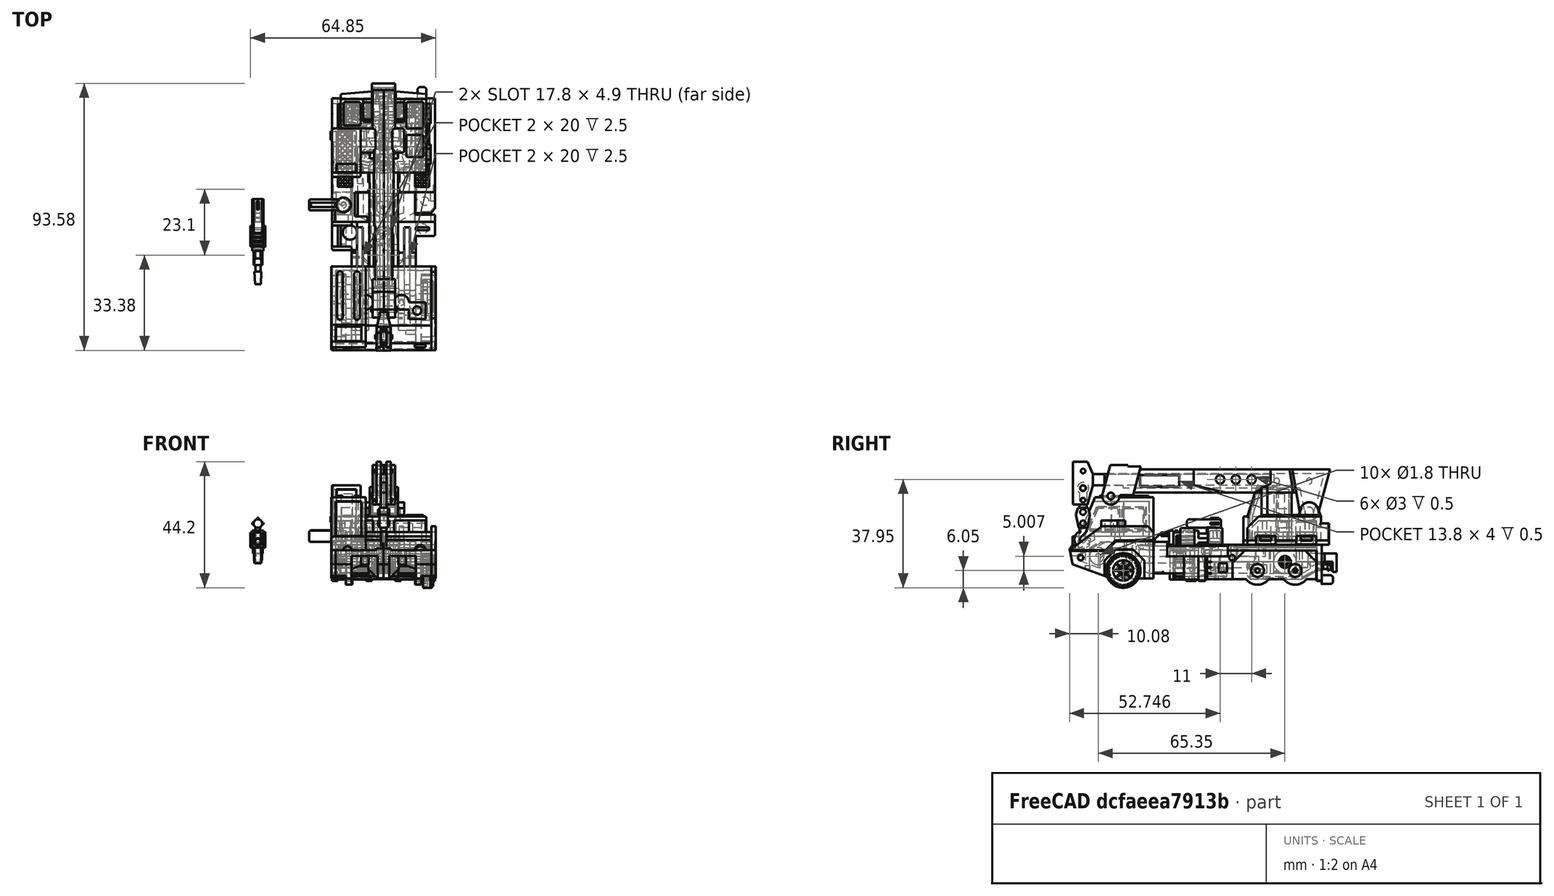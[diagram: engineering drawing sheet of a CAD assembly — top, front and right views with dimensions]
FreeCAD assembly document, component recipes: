
FREECAD ASSEMBLY — COMPONENT RECIPES ("Hook")

This assembly document has 27 components, labeled P0..P26 below (a component is one placed body or linked part). 27 of them carry a construction recipe — the FreeCAD feature program that regenerates the part from scratch, quoted from this document or its linked companion documents; the rest are supplied as boundary geometry only. No exploded tour is included for this assembly.
NOTE — document 3 of 5 of this assembly tour. The two overview renders and the header above are repeated from document 1; the component sections below continue where the previous document stopped.
COMPONENT P13 — recipe-attached ("Legs", modeled in this document).
Construction recipe (the document's own serialized feature program — sketch geometry with constraints, then the solid features built on it; lengths are millimeters unless a unit is written):

FEATURE [PartDesign::SubShapeBinder] Binder009
  BindCopyOnChange = 0
  BindMode = 0
  ClaimChildren = false
  Context = -> Part [Body015.Binder009.]
  Fuse = false
  MakeFace = true
  OffsetFill = false
  OffsetIntersection = false
  OffsetJoinType = 0
  OffsetOpenResult = false
  PartialLoad = false
  Refine = true
  Relative = true
  Support = -> [Body010[Fillet006.Face6]]
  _Version = 2
FEATURE [Sketcher::SketchObject] Sketch213
  ArcFitTolerance = 1e-06
  AttachmentSupport = -> [Binder009]
  ExternalGeometry = -> [Binder009]
  FullyConstrained = true
  MakeInternals = false
  MapMode = 5
  Placement = pos=(0,0,0) rot=(1,0,0;1.5708rad)
  sketch-geometry (4):
    g0: LineSegment StartX=12.75 StartY=-6 StartZ=0 EndX=23.25 EndY=-6 EndZ=0
    g1: LineSegment StartX=12.75 StartY=-6 StartZ=0 EndX=12.75 EndY=-2 EndZ=0
    g2: LineSegment StartX=12.75 StartY=-2 StartZ=0 EndX=23.25 EndY=-2 EndZ=0
    g3: LineSegment StartX=23.25 StartY=-2 StartZ=0 EndX=23.25 EndY=-6 EndZ=0
  constraints (11):
    c: Coincident(g0,g-7)
    c: Coincident(g0,g-8)
    c: DistanceX(g0,g0) = 10.5
    c: Coincident(g1,g0)
    c: Vertical(g1)
    c: DistanceY(g1,g1) = 4
    c: Coincident(g2,g1)
    c: Horizontal(g2)
    c: Coincident(g3,g2)
    c: Coincident(g3,g0)
    c: Vertical(g3)
FEATURE [PartDesign::Pad] Pad144
  Direction = (0,-1,2e-16)
  Length = 10
  Length2 = 10
  Profile = -> Sketch213
  ReferenceAxis = -> Sketch213 [N_Axis]
  Refine = true
  Suppressed = false
  Type = 0
FEATURE [Sketcher::SketchObject] Sketch214
  ArcFitTolerance = 1e-06
  AttachmentSupport = -> [Pad144]
  ExternalGeometry = -> [Pad144]
  FullyConstrained = true
  MakeInternals = false
  MapMode = 5
  Placement = pos=(0,-4e-16,-2) rot=(0,0,1;0rad)
  sketch-geometry (4):
    g0: LineSegment StartX=15 StartY=-2.25 StartZ=0 EndX=15 EndY=-8.25 EndZ=0
    g1: LineSegment StartX=15 StartY=-8.25 StartZ=0 EndX=21 EndY=-8.25 EndZ=0
    g2: LineSegment StartX=21 StartY=-8.25 StartZ=0 EndX=21 EndY=-2.25 EndZ=0
    g3: LineSegment StartX=21 StartY=-2.25 StartZ=0 EndX=15 EndY=-2.25 EndZ=0
  constraints (13):
    c: Coincident(g0,g1)
    c: Coincident(g1,g2)
    c: Coincident(g2,g3)
    c: Coincident(g3,g0)
    c: Vertical(g0)
    c: Vertical(g2)
    c: Horizontal(g1)
    c: Horizontal(g3)
    c: DistanceX(g3,g3) = 6
    c: DistanceX(g-3,g0) = 2.25
    c: DistanceX(g-4,g-4) = 10.5
    c: DistanceY(g0,g0) = 6
    c: DistanceY(g2,g-3) = 2.25
FEATURE [PartDesign::Pocket] Pocket096
  BaseFeature = -> Pad144
  Direction = (0,0,-1)
  Length = 2
  Length2 = 5
  Profile = -> Sketch214
  ReferenceAxis = -> Sketch214 [N_Axis]
  Refine = true
  Suppressed = false
  Type = 0
FEATURE [Sketcher::SketchObject] Sketch215
  ArcFitTolerance = 1e-06
  AttachmentSupport = -> [Pocket096]
  ExternalGeometry = -> [Pocket096]
  FullyConstrained = true
  MakeInternals = false
  MapMode = 5
  Placement = pos=(0,0,-4) rot=(0,0,1;0rad)
  sketch-geometry (1):
    g0: Circle CenterX=18 CenterY=-5.25 CenterZ=0 NormalX=0 NormalY=0 NormalZ=1 AngleXU=0 Radius=2.4
  constraints (3):
    c: Diameter(g0) = 4.8
    c: DistanceX(g-3,g0) = 3
    c: DistanceY(g0,g-3) = 3
FEATURE [PartDesign::Pad] Pad145
  BaseFeature = -> Pocket096
  Direction = (0,0,1)
  Length = 4.2
  Length2 = 10
  Profile = -> Sketch215
  ReferenceAxis = -> Sketch215 [N_Axis]
  Refine = true
  Suppressed = false
  Type = 0
FEATURE [Sketcher::SketchObject] Sketch216
  ArcFitTolerance = 1e-06
  AttachmentSupport = -> [Pad145]
  ExternalGeometry = -> [Pad145]
  FullyConstrained = true
  MakeInternals = false
  MapMode = 5
  Placement = pos=(0,0,0.2) rot=(0,0,1;0rad)
  sketch-geometry (1):
    g0: Circle CenterX=18 CenterY=-5.25 CenterZ=0 NormalX=0 NormalY=0 NormalZ=1 AngleXU=0 Radius=0.75
  constraints (2):
    c: Coincident(g0,g-3)
    c: Radius(g0) = 0.75
FEATURE [PartDesign::Pocket] Pocket097
  BaseFeature = -> Pad145
  Direction = (0,0,-1)
  Length = 7
  Length2 = 5
  Profile = -> Sketch216
  ReferenceAxis = -> Sketch216 [N_Axis]
  Refine = true
  Suppressed = false
  Type = 0
FEATURE [Sketcher::SketchObject] Sketch217
  ArcFitTolerance = 1e-06
  AttachmentSupport = -> [Pocket097]
  ExternalGeometry = -> [Pocket097]
  FullyConstrained = true
  MakeInternals = false
  MapMode = 5
  Placement = pos=(0,-4e-16,-2) rot=(0,0,1;0rad)
  sketch-geometry (8):
    g0: LineSegment StartX=23.25 StartY=0 StartZ=0 EndX=23.25 EndY=-24 EndZ=0
    g1: LineSegment StartX=23.25 StartY=-24 StartZ=0 EndX=29.25 EndY=-24 EndZ=0
    g2: LineSegment StartX=29.25 StartY=-24 StartZ=0 EndX=29.25 EndY=0 EndZ=0
    g3: LineSegment StartX=29.25 StartY=0 StartZ=0 EndX=23.25 EndY=0 EndZ=0
    g4: LineSegment StartX=12.75 StartY=0 StartZ=0 EndX=6.75 EndY=0 EndZ=0
    g5: LineSegment StartX=6.75 StartY=0 StartZ=0 EndX=6.75 EndY=-24 EndZ=0
    g6: LineSegment StartX=6.75 StartY=-24 StartZ=0 EndX=12.75 EndY=-24 EndZ=0
    g7: LineSegment StartX=12.75 StartY=-24 StartZ=0 EndX=12.75 EndY=0 EndZ=0
  constraints (22):
    c: Coincident(g0,g1)
    c: Coincident(g1,g2)
    c: Coincident(g2,g3)
    c: Coincident(g3,g0)
    c: Vertical(g0)
    c: Vertical(g2)
    c: Horizontal(g1)
    c: Horizontal(g3)
    c: Coincident(g0,g-3)
    c: Coincident(g4,g5)
    c: Coincident(g5,g6)
    c: Coincident(g6,g7)
    c: Coincident(g7,g4)
    c: Horizontal(g4)
    c: Horizontal(g6)
    c: Vertical(g5)
    c: Vertical(g7)
    c: Coincident(g4,g-4)
    c: DistanceX(g1,g1) = 6
    c: DistanceX(g6,g6) = 6
    c: DistanceY(g5,g5) = 24
    c: DistanceY(g2,g2) = 24
FEATURE [PartDesign::Pad] Pad146
  BaseFeature = -> Pocket097
  Direction = (0,0,1)
  Length = 6
  Length2 = 10
  Profile = -> Sketch217
  ReferenceAxis = -> Sketch217 [N_Axis]
  Refine = true
  Reversed = true
  Suppressed = false
  Type = 0
FEATURE [Sketcher::SketchObject] Sketch218
  ArcFitTolerance = 1e-06
  AttachmentSupport = -> [Pad146]
  ExternalGeometry = -> [Pad146]
  FullyConstrained = true
  MakeInternals = false
  MapMode = 5
  Placement = pos=(0,0,-2) rot=(0,0,1;0rad)
  sketch-geometry (8):
    g0: LineSegment StartX=6.75 StartY=-10.9 StartZ=0 EndX=6.75 EndY=-34.8 EndZ=0
    g1: LineSegment StartX=6.75 StartY=-34.8 StartZ=0 EndX=12.75 EndY=-34.8 EndZ=0
    g2: LineSegment StartX=12.75 StartY=-34.8 StartZ=0 EndX=12.75 EndY=-10.9 EndZ=0
    g3: LineSegment StartX=12.75 StartY=-10.9 StartZ=0 EndX=6.75 EndY=-10.9 EndZ=0
    g4: LineSegment StartX=29.25 StartY=-10.9 StartZ=0 EndX=23.25 EndY=-10.9 EndZ=0
    g5: LineSegment StartX=23.25 StartY=-10.9 StartZ=0 EndX=23.25 EndY=-34.8 EndZ=0
    g6: LineSegment StartX=23.25 StartY=-34.8 StartZ=0 EndX=29.25 EndY=-34.8 EndZ=0
    g7: LineSegment StartX=29.25 StartY=-34.8 StartZ=0 EndX=29.25 EndY=-10.9 EndZ=0
  constraints (24):
    c: Coincident(g0,g1)
    c: Coincident(g1,g2)
    c: Coincident(g2,g3)
    c: Coincident(g3,g0)
    c: Vertical(g0)
    c: Vertical(g2)
    c: Horizontal(g1)
    c: Horizontal(g3)
    c: Coincident(g4,g5)
    c: Coincident(g5,g6)
    c: Coincident(g6,g7)
    c: Coincident(g7,g4)
    c: Horizontal(g4)
    c: Horizontal(g6)
    c: Vertical(g5)
    c: Vertical(g7)
    c: PointOnObject(g4,g-3)
    c: PointOnObject(g4,g-4)
    c: PointOnObject(g2,g-5)
    c: DistanceY(g4,g-3) = 10.9
    c: DistanceY(g0,g0) = 23.9
    c: DistanceY(g7,g7) = 23.9
    c: DistanceY(g0,g-6) = 10.9
    c: PointOnObject(g-6,g0)
FEATURE [PartDesign::Pad] Pad147
  BaseFeature = -> Pad146
  Direction = (0,0,1)
  Length = 5
  Length2 = 10
  Profile = -> Sketch218
  ReferenceAxis = -> Sketch218 [N_Axis]
  Refine = true
  Suppressed = false
  Type = 0
FEATURE [Sketcher::SketchObject] Sketch219
  ArcFitTolerance = 1e-06
  AttachmentSupport = -> [Pad147]
  ExternalGeometry = -> [Pad147]
  FullyConstrained = true
  MakeInternals = false
  MapMode = 5
  Placement = pos=(29.25,0,0) rot=(0.57735,0.57735,0.57735;2.0944rad)
  sketch-geometry (3):
    g0: ArcOfCircle CenterX=-35 CenterY=-1.99333 CenterZ=0 NormalX=0 NormalY=0 NormalZ=1 AngleXU=0 Radius=3 StartAngle=1.50408 EndAngle=6.28096
    g1: LineSegment StartX=-32 StartY=-2 StartZ=0 EndX=-34.8 EndY=-2 EndZ=0
    g2: LineSegment StartX=-34.8 StartY=-2 StartZ=0 EndX=-34.8 EndY=1 EndZ=0
  constraints (9):
    c: PointOnObject(g0,g-3)
    c: PointOnObject(g0,g-4)
    c: Diameter(g0) = 6
    c: DistanceY(g0,g-4) = 2
    c: DistanceX(g0,g-3) = 8
    c: Coincident(g1,g0)
    c: Coincident(g1,g-4)
    c: Coincident(g2,g1)
    c: Coincident(g2,g0)
FEATURE [PartDesign::Pad] Pad148
  BaseFeature = -> Pad147
  Direction = (1,0,0)
  Length = 22.5
  Length2 = 10
  Profile = -> Sketch219
  ReferenceAxis = -> Sketch219 [N_Axis]
  Refine = true
  Reversed = true
  Suppressed = false
  Type = 0
FEATURE [Sketcher::SketchObject] Sketch220
  ArcFitTolerance = 1e-06
  AttachmentSupport = -> [Pad148]
  ExternalGeometry = -> [Pad148]
  FullyConstrained = true
  MakeInternals = false
  MapMode = 5
  Placement = pos=(0,0,3) rot=(0,0,1;0rad)
  sketch-geometry (4):
    g0: LineSegment StartX=12.75 StartY=-32 StartZ=0 EndX=12.75 EndY=-38 EndZ=0
    g1: LineSegment StartX=12.75 StartY=-38 StartZ=0 EndX=23.25 EndY=-38 EndZ=0
    g2: LineSegment StartX=23.25 StartY=-38 StartZ=0 EndX=23.25 EndY=-32 EndZ=0
    g3: LineSegment StartX=23.25 StartY=-32 StartZ=0 EndX=12.75 EndY=-32 EndZ=0
  constraints (10):
    c: Coincident(g0,g1)
    c: Coincident(g1,g2)
    c: Coincident(g2,g3)
    c: Coincident(g3,g0)
    c: Vertical(g0)
    c: Vertical(g2)
    c: Horizontal(g1)
    c: Coincident(g0,g-5)
    c: Coincident(g2,g-5)
    c: DistanceY(g2,g2) = 6
FEATURE [PartDesign::Pocket] Pocket098
  BaseFeature = -> Pad148
  Direction = (0,0,-1)
  Length = 8
  Length2 = 5
  Profile = -> Sketch220
  ReferenceAxis = -> Sketch220 [N_Axis]
  Refine = true
  Suppressed = false
  Type = 0
FEATURE [Sketcher::SketchObject] Sketch221
  ArcFitTolerance = 1e-06
  AttachmentSupport = -> [Pocket098]
  ExternalGeometry = -> [Pocket098]
  FullyConstrained = true
  MakeInternals = false
  MapMode = 5
  Placement = pos=(6.75,0,0) rot=(0.57735,-0.57735,-0.57735;2.0944rad)
  sketch-geometry (5):
    g0: LineSegment StartX=36.5 StartY=0.60475 StartZ=0 EndX=34.8 EndY=1.58624 EndZ=0
    g1: LineSegment [constr] StartX=35 StartY=-1.99333 StartZ=0 EndX=38 EndY=-1.99333 EndZ=0
    g2: LineSegment [constr] StartX=35 StartY=-1.99333 StartZ=0 EndX=36.5 EndY=0.60475 EndZ=0
    g3: LineSegment StartX=34.8 StartY=1.58624 StartZ=0 EndX=34.8 EndY=1 EndZ=0
    g4: ArcOfCircle CenterX=35 CenterY=-1.99333 CenterZ=0 NormalX=0 NormalY=0 NormalZ=1 AngleXU=0 Radius=3 StartAngle=1.0472 EndAngle=1.63751
  constraints (14):
    c: PointOnObject(g0,g-3)
    c: PointOnObject(g0,g-4)
    c: Angle(g-4,g0) = 1.0472
    c: Coincident(g1,g-3)
    c: PointOnObject(g1,g-3)
    c: Horizontal(g1)
    c: Coincident(g2,g0)
    c: Angle(g1,g2) = 1.0472
    c: Coincident(g2,g1)
    c: Coincident(g3,g0)
    c: Coincident(g3,g-4)
    c: Coincident(g4,g3)
    c: Coincident(g4,g0)
    c: Tangent(g4,g-3)
FEATURE [PartDesign::Pad] Pad149
  BaseFeature = -> Pocket098
  Direction = (-1,0,0)
  Length = 22.5
  Length2 = 10
  Profile = -> Sketch221
  ReferenceAxis = -> Sketch221 [N_Axis]
  Refine = true
  Reversed = true
  Suppressed = false
  Type = 0
FEATURE [Sketcher::SketchObject] Sketch222
  ArcFitTolerance = 1e-06
  AttachmentSupport = -> [Pad149]
  ExternalGeometry = -> [Pad149]
  FullyConstrained = true
  MakeInternals = false
  MapMode = 5
  Placement = pos=(0,0,3) rot=(0,0,1;0rad)
  sketch-geometry (4):
    g0: LineSegment StartX=12.75 StartY=-32 StartZ=0 EndX=12.75 EndY=-38 EndZ=0
    g1: LineSegment StartX=12.75 StartY=-38 StartZ=0 EndX=23.25 EndY=-38 EndZ=0
    g2: LineSegment StartX=23.25 StartY=-38 StartZ=0 EndX=23.25 EndY=-32 EndZ=0
    g3: LineSegment StartX=23.25 StartY=-32 StartZ=0 EndX=12.75 EndY=-32 EndZ=0
  constraints (10):
    c: Coincident(g0,g1)
    c: Coincident(g1,g2)
    c: Coincident(g2,g3)
    c: Coincident(g3,g0)
    c: Vertical(g0)
    c: Vertical(g2)
    c: Horizontal(g1)
    c: Horizontal(g3)
    c: Coincident(g0,g-5)
    c: Coincident(g1,g-4)
FEATURE [PartDesign::Pocket] Pocket099
  BaseFeature = -> Pad149
  Direction = (0,0,-1)
  Length = 5
  Length2 = 5
  Profile = -> Sketch222
  ReferenceAxis = -> Sketch222 [N_Axis]
  Refine = true
  Suppressed = false
  Type = 0
FEATURE [Sketcher::SketchObject] Sketch223
  ArcFitTolerance = 1e-06
  AttachmentSupport = -> [Pocket099]
  ExternalGeometry = -> [Pocket099]
  FullyConstrained = true
  MakeInternals = false
  MapMode = 5
  Placement = pos=(29.25,0,0) rot=(0.57735,0.57735,0.57735;2.0944rad)
  sketch-geometry (4):
    g0: LineSegment [constr] StartX=-35 StartY=-1.99333 StartZ=0 EndX=-38 EndY=-1.99333 EndZ=0
    g1: LineSegment StartX=-34.8 StartY=1.58624 StartZ=0 EndX=-32.3513 EndY=3 EndZ=0
    g2: LineSegment StartX=-32.3513 StartY=3 StartZ=0 EndX=-34.8 EndY=3 EndZ=0
    g3: LineSegment StartX=-34.8 StartY=3 StartZ=0 EndX=-34.8 EndY=1.58624 EndZ=0
  constraints (11):
    c: Coincident(g0,g-4)
    c: PointOnObject(g0,g-4)
    c: Horizontal(g0)
    c: DistanceX(g0,g-3) = 38
    c: Coincident(g1,g-5)
    c: PointOnObject(g1,g-6)
    c: Coincident(g2,g1)
    c: Coincident(g2,g-6)
    c: Coincident(g3,g2)
    c: Coincident(g3,g1)
    c: Angle(g-7,g1) = 3.14159
FEATURE [PartDesign::Pocket] Pocket100
  BaseFeature = -> Pocket099
  Direction = (-1,0,0)
  Length = 23
  Length2 = 5
  Profile = -> Sketch223
  ReferenceAxis = -> Sketch223 [N_Axis]
  Refine = true
  Suppressed = false
  Type = 0
FEATURE [Sketcher::SketchObject] Sketch224
  ArcFitTolerance = 1e-06
  AttachmentSupport = -> [Pocket100]
  ExternalGeometry = -> [Pocket100]
  FullyConstrained = true
  MakeInternals = false
  MapMode = 5
  Placement = pos=(29.25,0,0) rot=(0.57735,0.57735,0.57735;2.0944rad)
  sketch-geometry (4):
    g0: Circle CenterX=-35 CenterY=-1.99333 CenterZ=0 NormalX=0 NormalY=0 NormalZ=1 AngleXU=0 Radius=0.8
    g1: LineSegment StartX=-24 StartY=-8 StartZ=0 EndX=-24 EndY=-5.5 EndZ=0
    g2: LineSegment StartX=-24 StartY=-5.5 StartZ=0 EndX=-17.1313 EndY=-8 EndZ=0
    g3: LineSegment StartX=-24 StartY=-8 StartZ=0 EndX=-17.1313 EndY=-8 EndZ=0
  constraints (10):
    c: Coincident(g0,g-3)
    c: Radius(g0) = 0.8
    c: Coincident(g2,g1)
    c: PointOnObject(g1,g-4)
    c: DistanceY(g1,g-4) = 3.5
    c: Coincident(g3,g1)
    c: Coincident(g3,g2)
    c: Horizontal(g3)
    c: Coincident(g1,g-4)
    c: Angle(g1,g2) = 1.22173
FEATURE [PartDesign::Pocket] Pocket101
  BaseFeature = -> Pocket100
  Direction = (-1,0,0)
  Length = 23
  Length2 = 5
  Profile = -> Sketch224
  ReferenceAxis = -> Sketch224 [N_Axis]
  Refine = true
  Suppressed = false
  Type = 0
FEATURE [Sketcher::SketchObject] Sketch225
  ArcFitTolerance = 1e-06
  AttachmentSupport = -> [Pocket101]
  ExternalGeometry = -> [Pocket101]
  FullyConstrained = true
  MakeInternals = false
  MapMode = 5
  Placement = pos=(0,0,-2) rot=(1,0,0;3.14159rad)
  sketch-geometry (5):
    g0: ArcOfCircle CenterX=9.75 CenterY=24 CenterZ=0 NormalX=0 NormalY=0 NormalZ=1 AngleXU=0 Radius=1.25 StartAngle=-9e-16 EndAngle=3.14159
    g1: ArcOfCircle CenterX=26.25 CenterY=24 CenterZ=0 NormalX=0 NormalY=0 NormalZ=1 AngleXU=0 Radius=1.25 StartAngle=1.7e-15 EndAngle=3.14159
    g2: LineSegment [constr] StartX=26.25 StartY=24 StartZ=0 EndX=26.25 EndY=25.25 EndZ=0
    g3: LineSegment StartX=25 StartY=24 StartZ=0 EndX=27.5 EndY=24 EndZ=0
    g4: LineSegment StartX=8.5 StartY=24 StartZ=0 EndX=11 EndY=24 EndZ=0
  constraints (19):
    c: PointOnObject(g0,g-4)
    c: PointOnObject(g0,g-4)
    c: PointOnObject(g1,g-3)
    c: PointOnObject(g1,g-3)
    c: PointOnObject(g0,g-4)
    c: PointOnObject(g1,g-3)
    c: Diameter(g0) = 2.5
    c: Diameter(g1) = 2.5
    c: DistanceX(g-4,g-4) = 6
    c: DistanceX(g-4,g0) = 3
    c: DistanceX(g-3,g1) = 3
    c: Coincident(g2,g1)
    c: PointOnObject(g2,g1)
    c: Vertical(g2)
    c: DistanceY(g2,g-5) = 6.75
    c: Coincident(g3,g1)
    c: Coincident(g3,g1)
    c: Coincident(g4,g0)
    c: Coincident(g4,g0)
FEATURE [PartDesign::Pad] Pad150
  BaseFeature = -> Pocket101
  Direction = (0,0,-1)
  Length = 3.5
  Length2 = 10
  Profile = -> Sketch225
  ReferenceAxis = -> Sketch225 [N_Axis]
  Refine = true
  Suppressed = false
  Type = 0
FEATURE [Sketcher::SketchObject] Sketch226
  ArcFitTolerance = 1e-06
  AttachmentSupport = -> [Pad150]
  ExternalGeometry = -> [Pad150]
  FullyConstrained = true
  MakeInternals = false
  MapMode = 5
  Placement = pos=(0,0,3) rot=(0,0,1;0rad)
  sketch-geometry (8):
    g0: LineSegment StartX=8.75 StartY=-10.9 StartZ=0 EndX=8.75 EndY=-32.3513 EndZ=0
    g1: LineSegment StartX=8.75 StartY=-32.3513 StartZ=0 EndX=10.75 EndY=-32.3513 EndZ=0
    g2: LineSegment StartX=10.75 StartY=-32.3513 StartZ=0 EndX=10.75 EndY=-10.9 EndZ=0
    g3: LineSegment StartX=10.75 StartY=-10.9 StartZ=0 EndX=8.75 EndY=-10.9 EndZ=0
    g4: LineSegment StartX=25.25 StartY=-10.9 StartZ=0 EndX=25.25 EndY=-32.3513 EndZ=0
    g5: LineSegment StartX=25.25 StartY=-32.3513 StartZ=0 EndX=27.25 EndY=-32.3513 EndZ=0
    g6: LineSegment StartX=27.25 StartY=-32.3513 StartZ=0 EndX=27.25 EndY=-10.9 EndZ=0
    g7: LineSegment StartX=27.25 StartY=-10.9 StartZ=0 EndX=25.25 EndY=-10.9 EndZ=0
  constraints (26):
    c: Coincident(g0,g1)
    c: Coincident(g1,g2)
    c: Coincident(g2,g3)
    c: Coincident(g3,g0)
    c: Vertical(g0)
    c: Vertical(g2)
    c: Horizontal(g1)
    c: Horizontal(g3)
    c: PointOnObject(g0,g-6)
    c: Coincident(g4,g5)
    c: Coincident(g5,g6)
    c: Coincident(g6,g7)
    c: Coincident(g7,g4)
    c: Vertical(g4)
    c: Vertical(g6)
    c: Horizontal(g5)
    c: Horizontal(g7)
    c: PointOnObject(g4,g-3)
    c: DistanceX(g-3,g-3) = 6
    c: DistanceX(g7,g7) = 2
    c: DistanceX(g-3,g4) = 2
    c: DistanceX(g6,g-3) = 2
    c: DistanceX(g3,g3) = 2
    c: DistanceX(g-6,g0) = 2
    c: PointOnObject(g1,g-7)
    c: PointOnObject(g5,g-5)
FEATURE [PartDesign::Pocket] Pocket102
  BaseFeature = -> Pad150
  Direction = (0,0,-1)
  Length = 3
  Length2 = 5
  Profile = -> Sketch226
  ReferenceAxis = -> Sketch226 [N_Axis]
  Refine = true
  Suppressed = false
  Type = 0
FEATURE [Sketcher::SketchObject] Sketch227
  ArcFitTolerance = 1e-06
  AttachmentSupport = -> [Pocket102]
  ExternalGeometry = -> [Pocket102]
  FullyConstrained = true
  MakeInternals = false
  MapMode = 5
  Placement = pos=(29.25,0,0) rot=(0.57735,0.57735,0.57735;2.0944rad)
  sketch-geometry (4):
    g0: LineSegment StartX=-32.3513 StartY=3 StartZ=0 EndX=-32.3513 EndY=0 EndZ=0
    g1: ArcOfCircle CenterX=-35 CenterY=-1.99333 CenterZ=0 NormalX=0 NormalY=0 NormalZ=1 AngleXU=0 Radius=3 StartAngle=0.726747 EndAngle=2.0944
    g2: LineSegment StartX=-32.758 StartY=0 StartZ=0 EndX=-32.3513 EndY=0 EndZ=0
    g3: LineSegment StartX=-32.3513 StartY=3 StartZ=0 EndX=-36.5 EndY=0.60475 EndZ=0
  constraints (10):
    c: Radius(g-3) = 3
    c: Coincident(g0,g-4)
    c: Coincident(g0,g-4)
    c: Coincident(g1,g-3)
    c: Coincident(g1,g-3)
    c: Coincident(g2,g1)
    c: Coincident(g2,g0)
    c: Horizontal(g2)
    c: Coincident(g3,g0)
    c: Coincident(g3,g1)
FEATURE [PartDesign::Pocket] Pocket103
  BaseFeature = -> Pocket102
  Direction = (-1,0,0)
  Length = 4
  Length2 = 5
  Profile = -> Sketch227
  ReferenceAxis = -> Sketch227 [N_Axis]
  Refine = true
  Suppressed = false
  Type = 0
FEATURE [Sketcher::SketchObject] Sketch228
  ArcFitTolerance = 1e-06
  AttachmentSupport = -> [Pocket103]
  ExternalGeometry = -> [Pocket103]
  FullyConstrained = true
  MakeInternals = false
  MapMode = 5
  Placement = pos=(29.25,0,0) rot=(0.57735,0.57735,0.57735;2.0944rad)
  sketch-geometry (4):
    g0: LineSegment StartX=-32.3513 StartY=3 StartZ=0 EndX=-36.5 EndY=0.60475 EndZ=0
    g1: LineSegment StartX=-32.3513 StartY=3 StartZ=0 EndX=-32.3513 EndY=0 EndZ=0
    g2: LineSegment StartX=-32.3513 StartY=0 StartZ=0 EndX=-32.758 EndY=-4.41329e-11 EndZ=0
    g3: ArcOfCircle CenterX=-35 CenterY=-1.99332 CenterZ=0 NormalX=0 NormalY=0 NormalZ=1 AngleXU=0 Radius=2.99999 StartAngle=0.726746 EndAngle=2.0944
  constraints (9):
    c: Coincident(g0,g-3)
    c: Coincident(g0,g-5)
    c: Coincident(g1,g0)
    c: Coincident(g1,g-4)
    c: Coincident(g2,g1)
    c: Coincident(g2,g-5)
    c: Coincident(g3,g0)
    c: Coincident(g3,g2)
    c: Tangent(g3,g-5)
FEATURE [PartDesign::Pad] Pad151
  BaseFeature = -> Pocket103
  Direction = (1,0,0)
  Length = 2
  Length2 = 10
  Profile = -> Sketch228
  ReferenceAxis = -> Sketch228 [N_Axis]
  Refine = true
  Reversed = true
  Suppressed = false
  Type = 0
FEATURE [Sketcher::SketchObject] Sketch229
  ArcFitTolerance = 1e-06
  AttachmentSupport = -> [Pad151]
  ExternalGeometry = -> [Pad151]
  FullyConstrained = true
  MakeInternals = false
  MapMode = 5
  Placement = pos=(6.75,0,0) rot=(0.57735,-0.57735,-0.57735;2.0944rad)
  sketch-geometry (4):
    g0: ArcOfCircle CenterX=35 CenterY=-1.99333 CenterZ=0 NormalX=0 NormalY=0 NormalZ=1 AngleXU=0 Radius=3 StartAngle=1.0472 EndAngle=2.41485
    g1: LineSegment StartX=32.3513 StartY=3 StartZ=0 EndX=32.3513 EndY=0 EndZ=0
    g2: LineSegment StartX=32.3513 StartY=0 StartZ=0 EndX=32.758 EndY=0 EndZ=0
    g3: LineSegment StartX=32.3513 StartY=3 StartZ=0 EndX=36.5 EndY=0.60475 EndZ=0
  constraints (9):
    c: Coincident(g0,g-4)
    c: Coincident(g1,g-5)
    c: Coincident(g1,g-5)
    c: Coincident(g2,g1)
    c: Coincident(g2,g0)
    c: Horizontal(g2)
    c: Coincident(g0,g-3)
    c: Coincident(g3,g1)
    c: Coincident(g3,g0)
FEATURE [PartDesign::Pocket] Pocket104
  BaseFeature = -> Pad151
  Direction = (1,0,0)
  Length = 4
  Length2 = 5
  Profile = -> Sketch229
  ReferenceAxis = -> Sketch229 [N_Axis]
  Refine = true
  Suppressed = false
  Type = 0
FEATURE [Sketcher::SketchObject] Sketch230
  ArcFitTolerance = 1e-06
  AttachmentSupport = -> [Pocket104]
  ExternalGeometry = -> [Pocket104]
  FullyConstrained = true
  MakeInternals = false
  MapMode = 5
  Placement = pos=(6.75,0,0) rot=(0.57735,-0.57735,-0.57735;2.0944rad)
  sketch-geometry (4):
    g0: LineSegment StartX=32.3513 StartY=3 StartZ=0 EndX=32.3513 EndY=0 EndZ=0
    g1: LineSegment StartX=32.3513 StartY=0 StartZ=0 EndX=32.758 EndY=0 EndZ=0
    g2: LineSegment StartX=32.3513 StartY=3 StartZ=0 EndX=36.5 EndY=0.60475 EndZ=0
    g3: ArcOfCircle CenterX=35 CenterY=-1.99332 CenterZ=0 NormalX=0 NormalY=0 NormalZ=1 AngleXU=0 Radius=2.99999 StartAngle=1.0472 EndAngle=2.41485
  constraints (9):
    c: Coincident(g0,g-5)
    c: Coincident(g0,g-6)
    c: Coincident(g1,g0)
    c: Coincident(g1,g-6)
    c: Coincident(g2,g0)
    c: Coincident(g2,g-5)
    c: Coincident(g3,g1)
    c: Coincident(g3,g2)
    c: Tangent(g3,g-3)
FEATURE [PartDesign::Pad] Pad152
  BaseFeature = -> Pocket104
  Direction = (-1,0,0)
  Length = 2
  Length2 = 10
  Profile = -> Sketch230
  ReferenceAxis = -> Sketch230 [N_Axis]
  Refine = true
  Reversed = true
  Suppressed = false
  Type = 0
FEATURE [Sketcher::SketchObject] Sketch231
  ArcFitTolerance = 1e-06
  AttachmentSupport = -> [Pad152]
  ExternalGeometry = -> [Pad152]
  FullyConstrained = true
  MakeInternals = false
  MapMode = 5
  Placement = pos=(6.75,0,-1.7e-15) rot=(0.57735,-0.57735,-0.57735;2.0944rad)
  sketch-geometry (4):
    g0: LineSegment StartX=25.9 StartY=3 StartZ=0 EndX=25.9 EndY=1 EndZ=0
    g1: LineSegment StartX=25.9 StartY=1 StartZ=0 EndX=30.4 EndY=1 EndZ=0
    g2: LineSegment StartX=30.4 StartY=1 StartZ=0 EndX=30.4 EndY=3 EndZ=0
    g3: LineSegment StartX=30.4 StartY=3 StartZ=0 EndX=25.9 EndY=3 EndZ=0
  constraints (12):
    c: Coincident(g0,g1)
    c: Coincident(g1,g2)
    c: Coincident(g2,g3)
    c: Coincident(g3,g0)
    c: Vertical(g0)
    c: Vertical(g2)
    c: Horizontal(g1)
    c: Horizontal(g3)
    c: PointOnObject(g0,g-3)
    c: DistanceX(g3,g3) = 4.5
    c: DistanceX(g-3,g0) = 15
    c: DistanceY(g0,g0) = 2
FEATURE [PartDesign::Pocket] Pocket105
  BaseFeature = -> Pad152
  Direction = (1,0,0)
  Length = 23
  Length2 = 5
  Profile = -> Sketch231
  ReferenceAxis = -> Sketch231 [N_Axis]
  Refine = true
  Suppressed = false
  Type = 0
FEATURE [Sketcher::SketchObject] Sketch232
  ArcFitTolerance = 1e-06
  AttachmentSupport = -> [Pocket105]
  ExternalGeometry = -> [Pocket105]
  FullyConstrained = true
  MakeInternals = false
  MapMode = 5
  Placement = pos=(0,0,3) rot=(0,0,1;0rad)
  sketch-geometry (8):
    g0: LineSegment StartX=10.75 StartY=-22 StartZ=0 EndX=10.75 EndY=-2 EndZ=0
    g1: LineSegment StartX=10.75 StartY=-2 StartZ=0 EndX=8.75 EndY=-2 EndZ=0
    g2: LineSegment StartX=8.75 StartY=-2 StartZ=0 EndX=8.75 EndY=-22 EndZ=0
    g3: LineSegment StartX=8.75 StartY=-22 StartZ=0 EndX=10.75 EndY=-22 EndZ=0
    g4: LineSegment StartX=27.25 StartY=-22 StartZ=0 EndX=27.25 EndY=-2 EndZ=0
    g5: LineSegment StartX=27.25 StartY=-2 StartZ=0 EndX=25.25 EndY=-2 EndZ=0
    g6: LineSegment StartX=25.25 StartY=-2 StartZ=0 EndX=25.25 EndY=-22 EndZ=0
    g7: LineSegment StartX=25.25 StartY=-22 StartZ=0 EndX=27.25 EndY=-22 EndZ=0
  constraints (24):
    c: Coincident(g0,g1)
    c: Coincident(g1,g2)
    c: Coincident(g2,g3)
    c: Coincident(g3,g0)
    c: Vertical(g0)
    c: Vertical(g2)
    c: Horizontal(g1)
    c: Horizontal(g3)
    c: PointOnObject(g0,g-3)
    c: Coincident(g4,g5)
    c: Coincident(g5,g6)
    c: Coincident(g6,g7)
    c: Coincident(g7,g4)
    c: Vertical(g4)
    c: Vertical(g6)
    c: Horizontal(g5)
    c: Horizontal(g7)
    c: PointOnObject(g4,g-6)
    c: PointOnObject(g2,g-4)
    c: PointOnObject(g6,g-5)
    c: DistanceY(g-8,g4) = 2
    c: DistanceY(g-7,g2) = 2
    c: DistanceY(g1,g-1) = 2
    c: DistanceY(g5,g-1) = 2
FEATURE [PartDesign::Pocket] Pocket106
  BaseFeature = -> Pocket105
  Direction = (0,0,-1)
  Length = 7.5
  Length2 = 5
  Profile = -> Sketch232
  ReferenceAxis = -> Sketch232 [N_Axis]
  Refine = true
  Suppressed = false
  Type = 0
FEATURE [Sketcher::SketchObject] Sketch233
  ArcFitTolerance = 1e-06
  AttachmentSupport = -> [Pocket106]
  ExternalGeometry = -> [Pocket106]
  FullyConstrained = true
  MakeInternals = false
  MapMode = 5
  Placement = pos=(0,0,-8) rot=(1,0,0;3.14159rad)
  sketch-geometry (16):
    g0: LineSegment StartX=23.25 StartY=15.1313 StartZ=0 EndX=25.75 EndY=12.6313 EndZ=0
    g1: LineSegment StartX=25.75 StartY=12.6313 StartZ=0 EndX=29.25 EndY=12.6313 EndZ=0
    g2: LineSegment StartX=29.25 StartY=12.6313 StartZ=0 EndX=29.25 EndY=12.1313 EndZ=0
    g3: LineSegment StartX=29.25 StartY=12.1313 StartZ=0 EndX=25.5429 EndY=12.1313 EndZ=0
    g4: LineSegment StartX=25.5429 StartY=12.1313 StartZ=0 EndX=24.0429 EndY=13.6313 EndZ=0
    g5: LineSegment StartX=23.25 StartY=13.6313 StartZ=0 EndX=23.25 EndY=15.1313 EndZ=0
    g6: LineSegment StartX=24.0429 StartY=13.6313 StartZ=0 EndX=23.25 EndY=13.6313 EndZ=0
    g7: LineSegment [constr] StartX=25.3964 StartY=12.9849 StartZ=0 EndX=25.0429 EndY=12.6313 EndZ=0
    g8: LineSegment StartX=6.75 StartY=12.1313 StartZ=0 EndX=6.75 EndY=12.6313 EndZ=0
    g9: LineSegment StartX=6.75 StartY=12.6313 StartZ=0 EndX=10.25 EndY=12.6313 EndZ=0
    g10: LineSegment StartX=10.25 StartY=12.6313 StartZ=0 EndX=12.75 EndY=15.1313 EndZ=0
    g11: LineSegment StartX=6.75 StartY=12.1313 StartZ=0 EndX=10.4571 EndY=12.1313 EndZ=0
    g12: LineSegment StartX=10.4571 StartY=12.1313 StartZ=0 EndX=11.9571 EndY=13.6313 EndZ=0
    g13: LineSegment StartX=11.9571 StartY=13.6313 StartZ=0 EndX=12.75 EndY=13.6313 EndZ=0
    g14: LineSegment StartX=12.75 StartY=13.6313 StartZ=0 EndX=12.75 EndY=15.1313 EndZ=0
    g15: LineSegment [constr] StartX=10.9571 StartY=12.6313 StartZ=0 EndX=10.6036 EndY=12.9849 EndZ=0
  constraints (50):
    c: PointOnObject(g0,g-3)
    c: Coincident(g1,g0)
    c: PointOnObject(g1,g-4)
    c: Horizontal(g1)
    c: Coincident(g2,g1)
    c: PointOnObject(g2,g-4)
    c: Coincident(g3,g2)
    c: Horizontal(g3)
    c: Coincident(g4,g3)
    c: PointOnObject(g5,g-3)
    c: Coincident(g5,g0)
    c: Coincident(g6,g4)
    c: Coincident(g6,g5)
    c: Horizontal(g6)
    c: DistanceY(g2,g2) = 0.5
    c: DistanceY(g1,g-4) = 4.5
    c: Angle(g1,g0) = 2.35619
    c: Parallel(g4,g0)
    c: DistanceX(g0,g0) = 2.5
    c: PointOnObject(g7,g0)
    c: PointOnObject(g7,g4)
    c: Angle(g0,g7) = 1.5708
    c: Distance(g7) = 0.5
    c: Distance(g7,g0) = 0.5
    c: DistanceY(g5,g5) = 1.5
    c: PointOnObject(g8,g-6)
    c: PointOnObject(g8,g-6)
    c: Coincident(g9,g8)
    c: Horizontal(g9)
    c: Coincident(g10,g9)
    c: PointOnObject(g10,g-5)
    c: Coincident(g11,g8)
    c: Horizontal(g11)
    c: Coincident(g12,g11)
    c: Coincident(g13,g12)
    c: PointOnObject(g13,g-5)
    c: Horizontal(g13)
    c: Angle(g10,g9) = 2.35619
    c: Parallel(g12,g10)
    c: Coincident(g14,g13)
    c: Coincident(g14,g10)
    c: DistanceY(g14,g14) = 1.5
    c: DistanceY(g8,g-6) = 4.5
    c: DistanceY(g8,g8) = 0.5
    c: DistanceX(g9,g10) = 2.5
    c: PointOnObject(g15,g12)
    c: PointOnObject(g15,g10)
    c: Angle(g15,g12) = 1.5708
    c: Distance(g15,g9) = 0.5
    c: Distance(g15) = 0.5
FEATURE [PartDesign::Body] Body015  label="Legs"
  AllowCompound = false
  Group = -> [Binder009,Sketch213,Pad144,Sketch214,Pocket096,Sketch215,Pad145,Sketch216,Pocket097,Sketch217,Pad146,Sketch218,Pad147,Sketch219,Pad148,Sketch220,Pocket098,Sketch221,Pad149,Sketch222,Pocket099,Sketch223,Pocket100,Sketch224,Pocket101,Sketch225,Pad150,Sketch226,Pocket102,Sketch227,Pocket103,Sketch228,Pad151,Sketch229,Pocket104,Sketch230,Pad152,Sketch231,Pocket105,Sketch232,Pocket106,Sketch233,+33 more]
  Origin = -> Origin016
  Placement = pos=(0,8.9e-15,0) rot=(0,0,1;0rad)
  Tip = -> Pocket170
COMPONENT P14 — recipe-attached ("Right_Inner_Leg", modeled in this document).
Construction recipe (the document's own serialized feature program — sketch geometry with constraints, then the solid features built on it; lengths are millimeters unless a unit is written):

FEATURE [PartDesign::SubShapeBinder] Binder010
  BindCopyOnChange = 0
  BindMode = 2
  ClaimChildren = false
  Context = -> Body016 [Binder010.]
  Fuse = false
  MakeFace = true
  OffsetFill = false
  OffsetIntersection = false
  OffsetJoinType = 0
  OffsetOpenResult = false
  PartialLoad = false
  Refine = true
  Relative = true
  _Version = 2
FEATURE [Sketcher::SketchObject] Sketch246
  ArcFitTolerance = 1e-06
  AttachmentSupport = -> [Binder010]
  ExternalGeometry = -> [Binder010]
  FullyConstrained = true
  MakeInternals = false
  MapMode = 5
  Placement = pos=(29.25,0,-7.6e-15) rot=(0.57735,0.57735,0.57735;2.0944rad)
  sketch-geometry (13):
    g0: LineSegment StartX=-33.5313 StartY=3 StartZ=0 EndX=-17.1313 EndY=3 EndZ=0
    g1: LineSegment StartX=-17.1313 StartY=3 StartZ=0 EndX=-17.1313 EndY=-9.8 EndZ=0
    g2: LineSegment StartX=-17.1313 StartY=-9.8 StartZ=0 EndX=-22.1313 EndY=-9.8 EndZ=0
    g3: ArcOfCircle CenterX=-26.2738 CenterY=-7 CenterZ=0 NormalX=0 NormalY=0 NormalZ=1 AngleXU=0 Radius=5 StartAngle=3.73598 EndAngle=5.6888
    g4: LineSegment StartX=-30.4162 StartY=-9.8 StartZ=0 EndX=-44.062 EndY=-4.89651 EndZ=0
    g5: LineSegment StartX=-42.095 StartY=-1.94424 StartZ=0 EndX=-33.5313 EndY=3 EndZ=0
    g6: LineSegment [constr] StartX=-26.2738 StartY=-12 StartZ=0 EndX=-17.1313 EndY=-12 EndZ=0
    g7: LineSegment [constr] StartX=-17.1313 StartY=-9.8 StartZ=0 EndX=-17.1313 EndY=-12 EndZ=0
    g8: LineSegment [constr] StartX=-26.2738 StartY=-7 StartZ=0 EndX=-26.2738 EndY=-12 EndZ=0
    g9: LineSegment StartX=-42.095 StartY=-1.94424 StartZ=0 EndX=-44.595 EndY=-1.94424 EndZ=0
    g10: LineSegment StartX=-44.062 StartY=-4.89651 StartZ=0 EndX=-44.595 EndY=-1.94424 EndZ=0
    g11: Circle CenterX=-35 CenterY=-1.99333 CenterZ=0 NormalX=0 NormalY=0 NormalZ=1 AngleXU=0 Radius=0.8
    g12: Circle CenterX=-26.2738 CenterY=-7 CenterZ=0 NormalX=0 NormalY=0 NormalZ=1 AngleXU=0 Radius=0.8
  constraints (41):
    c: Horizontal(g0)
    c: Coincident(g1,g0)
    c: Vertical(g1)
    c: Coincident(g2,g1)
    c: Horizontal(g2)
    c: Coincident(g3,g2)
    c: Coincident(g4,g3)
    c: Coincident(g5,g0)
    c: Radius(g3) = 5
    c: DistanceY(g1,g1) = 12.8
    c: DistanceY(g2,g3) = 0
    c: PointOnObject(g6,g3)
    c: Horizontal(g6)
    c: Coincident(g7,g1)
    c: Coincident(g7,g6)
    c: Vertical(g7)
    c: DistanceY(g7,g7) = 2.2
    c: PointOnObject(g-3,g1)
    c: PointOnObject(g0,g-4)
    c: DistanceX(g0,g0) = 16.4
    c: Parallel(g5,g-5)
    c: Coincident(g8,g3)
    c: Coincident(g8,g6)
    c: Vertical(g8)
    c: Coincident(g9,g5)
    c: Horizontal(g9)
    c: Coincident(g10,g4)
    c: Coincident(g10,g9)
    c: Distance(g4) = 14.5
    c: DistanceX(g9,g9) = 2.5
    c: Angle(g4,g10) = 2.0944
    c: Distance(g10) = 3
    c: DistanceX(g2,g2) = 5
    c: DistanceX(g4,g1) = 26.9307
    c: DistanceX(g9,g0) = 27.4637
    c: DistanceX(g-6,g0) = 17.8687
    c: DistanceY(g5,g0) = 4.94424
    c: Coincident(g11,g-6)
    c: Equal(g11,g-6)
    c: Coincident(g12,g3)
    c: Radius(g12) = 0.8
FEATURE [PartDesign::Pad] Pad161
  Direction = (1,0,0)
  Length = 2
  Length2 = 10
  Profile = -> Sketch246
  ReferenceAxis = -> Sketch246 [N_Axis]
  Refine = true
  Suppressed = false
  Type = 0
FEATURE [Sketcher::SketchObject] Sketch247
  ArcFitTolerance = 1e-06
  AttachmentSupport = -> [Pad161]
  ExternalGeometry = -> [Pad161]
  FullyConstrained = true
  MakeInternals = false
  MapMode = 5
  Placement = pos=(31.25,0,0) rot=(0.57735,0.57735,0.57735;2.0944rad)
  sketch-geometry (10):
    g0: LineSegment StartX=-17.1313 StartY=3 StartZ=0 EndX=-33.5313 EndY=3 EndZ=0
    g1: LineSegment StartX=-33.5313 StartY=3 StartZ=0 EndX=-42.095 EndY=-1.94424 EndZ=0
    g2: LineSegment StartX=-17.1313 StartY=3 StartZ=0 EndX=-17.1313 EndY=5 EndZ=0
    g3: LineSegment StartX=-17.1313 StartY=5 StartZ=0 EndX=-36.4313 EndY=5 EndZ=0
    g4: LineSegment StartX=-36.4313 StartY=5 StartZ=0 EndX=-36.4313 EndY=3.63509 EndZ=0
    g5: LineSegment StartX=-36.4313 StartY=3.63509 StartZ=0 EndX=-42.6309 EndY=0.0557565 EndZ=0
    g6: LineSegment StartX=-42.6309 StartY=0.0557565 StartZ=0 EndX=-44.9561 EndY=0.0557565 EndZ=0
    g7: LineSegment StartX=-44.595 StartY=-1.94424 StartZ=0 EndX=-44.9561 EndY=0.0557565 EndZ=0
    g8: LineSegment [constr] StartX=-36.7303 StartY=1.15303 StartZ=0 EndX=-37.7303 EndY=2.88509 EndZ=0
    g9: LineSegment StartX=-42.095 StartY=-1.94424 StartZ=0 EndX=-44.595 EndY=-1.94424 EndZ=0
  constraints (27):
    c: Coincident(g0,g-4)
    c: Coincident(g0,g-5)
    c: Coincident(g1,g0)
    c: Coincident(g1,g-6)
    c: Coincident(g2,g0)
    c: Vertical(g2)
    c: Coincident(g3,g2)
    c: Horizontal(g3)
    c: DistanceX(g3,g3) = 19.3
    c: DistanceY(g2,g2) = 2
    c: Coincident(g4,g3)
    c: Vertical(g4)
    c: Coincident(g5,g4)
    c: Coincident(g6,g5)
    c: Coincident(g7,g-7)
    c: Coincident(g7,g6)
    c: DistanceY(g1,g5) = 2
    c: PointOnObject(g8,g1)
    c: PointOnObject(g8,g5)
    c: Angle(g8,g1) = 1.5708
    c: Parallel(g1,g5)
    c: Horizontal(g6)
    c: Distance(g8) = 2
    c: Angle(g7,g-7) = 3.14159
    c: Coincident(g9,g1)
    c: Coincident(g9,g7)
    c: Distance(g4,g8) = 1.5
FEATURE [PartDesign::Pad] Pad162
  BaseFeature = -> Pad161
  Direction = (1,0,0)
  Length = 13.25
  Length2 = 10
  Profile = -> Sketch247
  ReferenceAxis = -> Sketch247 [N_Axis]
  Refine = true
  Reversed = true
  Suppressed = false
  Type = 0
FEATURE [Sketcher::SketchObject] Sketch248
  ArcFitTolerance = 1e-06
  AttachmentSupport = -> [Pad162]
  ExternalGeometry = -> [Pad162]
  FullyConstrained = true
  MakeInternals = false
  MapMode = 5
  Placement = pos=(18,0,0) rot=(0.57735,-0.57735,-0.57735;2.0944rad)
  sketch-geometry (9):
    g0: LineSegment StartX=33.5313 StartY=3 StartZ=0 EndX=42.095 EndY=-1.94424 EndZ=0
    g1: LineSegment StartX=42.095 StartY=-1.94424 StartZ=0 EndX=44.595 EndY=-1.94424 EndZ=0
    g2: LineSegment StartX=44.595 StartY=-1.94424 StartZ=0 EndX=44.062 EndY=-4.89651 EndZ=0
    g3: LineSegment StartX=44.062 StartY=-4.89651 StartZ=0 EndX=30.4162 EndY=-9.8 EndZ=0
    g4: LineSegment StartX=30.4162 StartY=-9.8 StartZ=0 EndX=22.1313 EndY=-9.8 EndZ=0
    g5: LineSegment StartX=22.1313 StartY=-9.8 StartZ=0 EndX=19.2313 EndY=-2 EndZ=0
    g6: LineSegment StartX=19.2313 StartY=-2 StartZ=0 EndX=23.2313 EndY=-2 EndZ=0
    g7: LineSegment StartX=23.2313 StartY=-2 StartZ=0 EndX=23.2313 EndY=3 EndZ=0
    g8: LineSegment StartX=33.5313 StartY=3 StartZ=0 EndX=23.2313 EndY=3 EndZ=0
  constraints (21):
    c: Coincident(g0,g-8)
    c: Coincident(g1,g0)
    c: Coincident(g1,g-8)
    c: Coincident(g2,g1)
    c: Coincident(g2,g-4)
    c: Coincident(g3,g2)
    c: Coincident(g3,g-4)
    c: Coincident(g4,g3)
    c: Coincident(g5,g4)
    c: Coincident(g6,g5)
    c: Horizontal(g6)
    c: Coincident(g7,g6)
    c: Vertical(g7)
    c: Coincident(g8,g0)
    c: PointOnObject(g8,g-6)
    c: Coincident(g7,g8)
    c: DistanceY(g7,g7) = 5
    c: DistanceX(g-9,g7) = 6.1
    c: DistanceX(g6,g6) = 4
    c: Coincident(g0,g-7)
    c: Coincident(g4,g-5)
FEATURE [PartDesign::Pad] Pad163
  BaseFeature = -> Pad162
  Direction = (-1,0,0)
  Length = 2
  Length2 = 10
  Profile = -> Sketch248
  ReferenceAxis = -> Sketch248 [N_Axis]
  Refine = true
  Reversed = true
  Suppressed = false
  Type = 0
FEATURE [Sketcher::SketchObject] Sketch249
  ArcFitTolerance = 1e-06
  AttachmentSupport = -> [Pad163]
  ExternalGeometry = -> [Pad163]
  FullyConstrained = true
  MakeInternals = false
  MapMode = 5
  Placement = pos=(20,0,0) rot=(0.57735,0.57735,0.57735;2.0944rad)
  sketch-geometry (4):
    g0: LineSegment StartX=-23.2313 StartY=3 StartZ=0 EndX=-25.2313 EndY=3 EndZ=0
    g1: LineSegment StartX=-25.2313 StartY=3 StartZ=0 EndX=-25.2313 EndY=-9.8 EndZ=0
    g2: LineSegment StartX=-25.2313 StartY=-9.8 StartZ=0 EndX=-23.2313 EndY=-9.8 EndZ=0
    g3: LineSegment StartX=-23.2313 StartY=-9.8 StartZ=0 EndX=-23.2313 EndY=3 EndZ=0
  constraints (11):
    c: Coincident(g0,g1)
    c: Coincident(g1,g2)
    c: Coincident(g2,g3)
    c: Coincident(g3,g0)
    c: Horizontal(g0)
    c: Horizontal(g2)
    c: Vertical(g1)
    c: Vertical(g3)
    c: Coincident(g0,g-3)
    c: PointOnObject(g1,g-4)
    c: DistanceX(g2,g2) = 2
FEATURE [PartDesign::Pad] Pad164
  BaseFeature = -> Pad163
  Direction = (1,0,0)
  Length = 3.3
  Length2 = 10
  Profile = -> Sketch249
  ReferenceAxis = -> Sketch249 [N_Axis]
  Refine = true
  Suppressed = false
  Type = 0
FEATURE [Sketcher::SketchObject] Sketch250
  ArcFitTolerance = 1e-06
  AttachmentSupport = -> [Pad164]
  ExternalGeometry = -> [Pad164]
  FullyConstrained = true
  MakeInternals = false
  MapMode = 5
  Placement = pos=(0,-23.2313,0) rot=(0,0.707107,0.707107;3.14159rad)
  sketch-geometry (3):
    g0: LineSegment StartX=-20 StartY=-9.8 StartZ=0 EndX=-23.3 EndY=-9.8 EndZ=0
    g1: LineSegment StartX=-23.3 StartY=-9.8 StartZ=0 EndX=-23.3 EndY=-6.5 EndZ=0
    g2: LineSegment StartX=-20 StartY=-9.8 StartZ=0 EndX=-23.3 EndY=-6.5 EndZ=0
  constraints (7):
    c: Coincident(g0,g-3)
    c: Coincident(g0,g-4)
    c: Coincident(g1,g0)
    c: PointOnObject(g1,g-4)
    c: Coincident(g2,g0)
    c: Coincident(g2,g1)
    c: Angle(g2,g0) = 0.785398
FEATURE [PartDesign::Pocket] Pocket114
  BaseFeature = -> Pad164
  Direction = (0,-1,2e-16)
  Length = 5
  Length2 = 5
  Profile = -> Sketch250
  ReferenceAxis = -> Sketch250 [N_Axis]
  Refine = true
  Suppressed = false
  Type = 0
FEATURE [Sketcher::SketchObject] Sketch251
  ArcFitTolerance = 1e-06
  AttachmentSupport = -> [Pocket114]
  ExternalGeometry = -> [Pocket114]
  FullyConstrained = true
  MakeInternals = false
  MapMode = 5
  Placement = pos=(20,0,0) rot=(0.57735,0.57735,0.57735;2.0944rad)
  sketch-geometry (1):
    g0: Circle CenterX=-35 CenterY=-1.99333 CenterZ=0 NormalX=0 NormalY=0 NormalZ=1 AngleXU=0 Radius=0.8
  constraints (2):
    c: Coincident(g0,g-3)
    c: Equal(g0,g-3)
FEATURE [PartDesign::Pocket] Pocket115
  BaseFeature = -> Pocket114
  Direction = (-1,0,0)
  Length = 5
  Length2 = 5
  Profile = -> Sketch251
  ReferenceAxis = -> Sketch251 [N_Axis]
  Refine = true
  Suppressed = false
  Type = 0
FEATURE [Sketcher::SketchObject] Sketch252
  ArcFitTolerance = 1e-06
  AttachmentSupport = -> [Pocket115]
  ExternalGeometry = -> [Pocket115]
  FullyConstrained = true
  MakeInternals = false
  MapMode = 5
  Placement = pos=(29.25,0,0) rot=(0.57735,-0.57735,-0.57735;2.0944rad)
  sketch-geometry (6):
    g0: LineSegment StartX=39.505 StartY=-0.448906 StartZ=0 EndX=39.505 EndY=-6.44891 EndZ=0
    g1: LineSegment StartX=39.505 StartY=-6.44891 StartZ=0 EndX=38.005 EndY=-6.44891 EndZ=0
    g2: LineSegment StartX=38.005 StartY=-6.44891 StartZ=0 EndX=38.005 EndY=0.417119 EndZ=0
    g3: LineSegment StartX=39.505 StartY=-0.448906 StartZ=0 EndX=38.005 EndY=0.417119 EndZ=0
    g4: GeomPoint [constr] X=39.505 Y=-6.44891 Z=0
    g5: GeomPoint [constr] X=38.005 Y=-6.44891 Z=0
  constraints (14):
    c: PointOnObject(g0,g-3)
    c: Vertical(g0)
    c: Horizontal(g1)
    c: Vertical(g2)
    c: Coincident(g3,g0)
    c: Coincident(g3,g2)
    c: DistanceX(g5,g4) = 1.5
    c: PointOnObject(g2,g-3)
    c: DistanceX(g0,g-3) = 2.59
    c: DistanceY(g0,g0) = 6
    c: Coincident(g1,g5)
    c: Coincident(g2,g1)
    c: Coincident(g1,g4)
    c: Coincident(g0,g1)
FEATURE [PartDesign::Pad] Pad165
  BaseFeature = -> Pocket115
  Direction = (-1,0,0)
  Length = 3.3
  Length2 = 10
  Profile = -> Sketch252
  ReferenceAxis = -> Sketch252 [N_Axis]
  Refine = true
  Suppressed = false
  Type = 0
FEATURE [Sketcher::SketchObject] Sketch253
  ArcFitTolerance = 1e-06
  AttachmentSupport = -> [Pad165]
  ExternalGeometry = -> [Pad165]
  FullyConstrained = true
  MakeInternals = false
  MapMode = 5
  Placement = pos=(0,-38.005,0) rot=(0,0.707107,0.707107;3.14159rad)
  sketch-geometry (3):
    g0: LineSegment StartX=-29.25 StartY=-6.44891 StartZ=0 EndX=-25.95 EndY=-6.44891 EndZ=0
    g1: LineSegment StartX=-25.95 StartY=-6.44891 StartZ=0 EndX=-25.95 EndY=-5.2478 EndZ=0
    g2: LineSegment StartX=-25.95 StartY=-5.2478 StartZ=0 EndX=-29.25 EndY=-6.44891 EndZ=0
  constraints (7):
    c: Coincident(g0,g-4)
    c: Coincident(g0,g-4)
    c: Coincident(g1,g-3)
    c: PointOnObject(g1,g-3)
    c: Coincident(g2,g1)
    c: Coincident(g2,g-4)
    c: Angle(g0,g2) = 0.349066
FEATURE [PartDesign::Pocket] Pocket116
  BaseFeature = -> Pad165
  Direction = (0,-1,2e-16)
  Length = 5
  Length2 = 5
  Profile = -> Sketch253
  ReferenceAxis = -> Sketch253 [N_Axis]
  Refine = true
  Suppressed = false
  Type = 0
FEATURE [Sketcher::SketchObject] Sketch254
  ArcFitTolerance = 1e-06
  AttachmentSupport = -> [Pocket116]
  ExternalGeometry = -> [Pocket116]
  FullyConstrained = true
  MakeInternals = false
  MapMode = 5
  Placement = pos=(0,0,5) rot=(0,0,1;0rad)
  sketch-geometry (1):
    g0: Circle CenterX=24.25 CenterY=-28.2313 CenterZ=0 NormalX=0 NormalY=0 NormalZ=1 AngleXU=0 Radius=1
  constraints (3):
    c: Radius(g0) = 1
    c: DistanceX(g-5,g0) = 6.25
    c: DistanceY(g0,g-5) = 11.1
FEATURE [PartDesign::Pocket] Pocket117
  BaseFeature = -> Pocket116
  Direction = (0,0,-1)
  Length = 5
  Length2 = 5
  Profile = -> Sketch254
  ReferenceAxis = -> Sketch254 [N_Axis]
  Refine = true
  Suppressed = false
  Type = 0
FEATURE [Sketcher::SketchObject] Sketch255
  ArcFitTolerance = 1e-06
  AttachmentSupport = -> [Pocket117]
  ExternalGeometry = -> [Pocket117]
  FullyConstrained = true
  MakeInternals = false
  MapMode = 5
  Placement = pos=(31.25,0,0) rot=(0.57735,0.57735,0.57735;2.0944rad)
  sketch-geometry (24):
    g0: LineSegment StartX=-36.4313 StartY=5 StartZ=0 EndX=-17.1313 EndY=5 EndZ=0
    g1: LineSegment StartX=-17.1313 StartY=5 StartZ=0 EndX=-17.1313 EndY=-9.8 EndZ=0
    g2: LineSegment StartX=-36.4313 StartY=5 StartZ=0 EndX=-36.4313 EndY=3.63509 EndZ=0
    g3: LineSegment StartX=-36.4313 StartY=3.63509 StartZ=0 EndX=-42.6309 EndY=0.0557565 EndZ=0
    g4: LineSegment StartX=-42.6309 StartY=0.0557565 StartZ=0 EndX=-44.9561 EndY=0.0557565 EndZ=0
    g5: LineSegment StartX=-44.9561 StartY=0.0557565 StartZ=0 EndX=-44.062 EndY=-4.89651 EndZ=0
    g6: LineSegment StartX=-44.062 StartY=-4.89651 StartZ=0 EndX=-32.8313 EndY=-8.93216 EndZ=0
    g7: LineSegment StartX=-32.8313 StartY=-8.93216 StartZ=0 EndX=-32.8313 EndY=-3.6 EndZ=0
    g8: LineSegment StartX=-32.8313 StartY=-3.6 StartZ=0 EndX=-28.8813 EndY=0.35 EndZ=0
    g9: LineSegment StartX=-28.8813 StartY=0.35 StartZ=0 EndX=-22.7813 EndY=0.35 EndZ=0
    g10: LineSegment StartX=-22.7813 StartY=0.35 StartZ=0 EndX=-18.8313 EndY=-3.6 EndZ=0
    g11: LineSegment StartX=-18.8313 StartY=-3.6 StartZ=0 EndX=-18.8313 EndY=-9.8 EndZ=0
    g12: LineSegment StartX=-17.1313 StartY=-9.8 StartZ=0 EndX=-18.8313 EndY=-9.8 EndZ=0
    g13: LineSegment StartX=-34.5313 StartY=3 StartZ=0 EndX=-28.6355 EndY=3 EndZ=0
    g14: LineSegment StartX=-28.6355 StartY=3 StartZ=0 EndX=-34.5313 EndY=-2.89584 EndZ=0
    g15: LineSegment StartX=-34.5313 StartY=-2.89584 StartZ=0 EndX=-34.5313 EndY=-6.19607 EndZ=0
    g16: LineSegment StartX=-34.5313 StartY=-6.19607 StartZ=0 EndX=-41.7556 EndY=-3.60007 EndZ=0
    g17: LineSegment StartX=-42.1528 StartY=-1.40026 StartZ=0 EndX=-34.5313 EndY=3 EndZ=0
    g18: Circle CenterX=-19.7813 CenterY=2.15 CenterZ=0 NormalX=0 NormalY=0 NormalZ=1 AngleXU=0 Radius=1.45
    g19: LineSegment [constr] StartX=-29.5884 StartY=-0.357107 StartZ=0 EndX=-30.7905 EndY=0.844975 EndZ=0
    g20: LineSegment [constr] StartX=-36.5473 StartY=1.83605 StartZ=0 EndX=-37.2973 EndY=3.13509 EndZ=0
    g21: LineSegment [constr] StartX=-40.8145 StartY=-3.93824 StartZ=0 EndX=-41.4909 EndY=-5.82041 EndZ=0
    g22: LineSegment StartX=-41.7556 StartY=-3.60007 StartZ=0 EndX=-42.1528 EndY=-1.40026 EndZ=0
    g23: LineSegment [constr] StartX=-41.9751 StartY=-2.38435 StartZ=0 EndX=-44.4353 EndY=-2.82854 EndZ=0
  constraints (69):
    c: Coincident(g0,g-4)
    c: Coincident(g0,g-10)
    c: Coincident(g1,g0)
    c: Coincident(g1,g-10)
    c: Coincident(g2,g0)
    c: Coincident(g2,g-5)
    c: Coincident(g3,g2)
    c: Coincident(g3,g-6)
    c: Coincident(g4,g3)
    c: Coincident(g4,g-7)
    c: Coincident(g5,g4)
    c: Coincident(g5,g-8)
    c: Coincident(g6,g5)
    c: PointOnObject(g6,g-8)
    c: Coincident(g7,g6)
    c: Vertical(g7)
    c: Coincident(g8,g7)
    c: Coincident(g9,g8)
    c: Horizontal(g9)
    c: Coincident(g10,g9)
    c: Coincident(g11,g10)
    c: PointOnObject(g11,g-9)
    c: Vertical(g11)
    c: Coincident(g12,g1)
    c: Coincident(g12,g11)
    c: Horizontal(g13)
    c: Coincident(g14,g13)
    c: Coincident(g15,g14)
    c: Vertical(g15)
    c: Coincident(g16,g15)
    c: Coincident(g17,g13)
    c: Diameter(g18) = 2.9
    c: DistanceX(g18,g0) = 2.65
    c: DistanceY(g18,g0) = 2.85
    c: DistanceX(g12,g12) = 1.7
    c: Angle(g10,g11) = 2.35619
    c: Angle(g8,g9) = 2.35619
    c: DistanceX(g9,g9) = 6.1
    c: DistanceY(g11,g11) = 6.2
    c: DistanceY(g7,g10) = 0
    c: DistanceX(g6,g11) = 14
    c: Parallel(g8,g14)
    c: PointOnObject(g19,g8)
    c: PointOnObject(g19,g14)
    c: Angle(g19,g8) = 1.5708
    c: Distance(g19) = 1.7
    c: Distance(g8,g19) = 1
    c: Parallel(g17,g3)
    c: Parallel(g16,g6)
    c: PointOnObject(g20,g17)
    c: PointOnObject(g20,g3)
    c: PointOnObject(g21,g16)
    c: PointOnObject(g21,g6)
    c: Angle(g21,g16) = 1.5708
    c: Angle(g3,g20) = 1.5708
    c: Distance(g20,g2) = 1
    c: Distance(g21,g16) = 1
    c: Distance(g21) = 2
    c: Distance(g20) = 1.5
    c: DistanceY(g13,g0) = 2
    c: DistanceX(g15,g7) = 1.7
    c: Coincident(g22,g16)
    c: Coincident(g22,g17)
    c: Parallel(g5,g22)
    c: PointOnObject(g23,g22)
    c: PointOnObject(g23,g5)
    c: Angle(g23,g22) = 1.5708
    c: Distance(g23) = 2.5
    c: Distance(g23,g17) = 1
FEATURE [PartDesign::Pad] Pad166
  BaseFeature = -> Pocket117
  Direction = (1,0,0)
  Length = 3.5
  Length2 = 10
  Profile = -> Sketch255
  ReferenceAxis = -> Sketch255 [N_Axis]
  Refine = true
  Suppressed = false
  Type = 0
FEATURE [Sketcher::SketchObject] Sketch256
  ArcFitTolerance = 1e-06
  AttachmentSupport = -> [Pad166]
  ExternalGeometry = -> [Pad166]
  FullyConstrained = true
  MakeInternals = false
  MapMode = 5
  Placement = pos=(34.75,0,0) rot=(0.57735,0.57735,0.57735;2.0944rad)
  sketch-geometry (1):
    g0: Circle CenterX=-35 CenterY=-1.99333 CenterZ=0 NormalX=0 NormalY=0 NormalZ=1 AngleXU=0 Radius=2
  constraints (3):
    c: Radius(g-3) = 0.8
    c: Coincident(g0,g-3)
    c: Radius(g0) = 2
FEATURE [PartDesign::Pocket] Pocket118
  BaseFeature = -> Pad166
  Direction = (-1,0,0)
  Length = 1.5
  Length2 = 5
  Profile = -> Sketch256
  ReferenceAxis = -> Sketch256 [N_Axis]
  Refine = true
  Suppressed = false
  Type = 0
FEATURE [Sketcher::SketchObject] Sketch257
  ArcFitTolerance = 1e-06
  AttachmentSupport = -> [Pocket118]
  ExternalGeometry = -> [Pocket118]
  FullyConstrained = true
  MakeInternals = false
  MapMode = 5
  Placement = pos=(31.25,0,0) rot=(0.57735,0.57735,0.57735;2.0944rad)
  sketch-geometry (2):
    g0: Circle CenterX=-26.2738 CenterY=-7 CenterZ=0 NormalX=0 NormalY=0 NormalZ=1 AngleXU=0 Radius=0.8
    g1: Circle CenterX=-26.2738 CenterY=-7 CenterZ=0 NormalX=0 NormalY=0 NormalZ=1 AngleXU=0 Radius=2.25
  constraints (4):
    c: Coincident(g0,g-3)
    c: Equal(g0,g-3)
    c: Coincident(g1,g0)
    c: Radius(g1) = 2.25
FEATURE [PartDesign::Pad] Pad167
  BaseFeature = -> Pocket118
  Direction = (1,0,0)
  Length = 2
  Length2 = 10
  Profile = -> Sketch257
  ReferenceAxis = -> Sketch257 [N_Axis]
  Refine = true
  Suppressed = false
  Type = 0
FEATURE [Sketcher::SketchObject] Sketch258
  ArcFitTolerance = 1e-06
  AttachmentSupport = -> [Pad167]
  ExternalGeometry = -> [Pad167]
  FullyConstrained = false
  MakeInternals = false
  MapMode = 5
  Placement = pos=(31.25,0,0) rot=(0.57735,0.57735,0.57735;2.0944rad)
  sketch-geometry (3):
    g0: Circle CenterX=-41.1657 CenterY=-2.53692 CenterZ=0 NormalX=0 NormalY=0 NormalZ=1 AngleXU=0 Radius=0.9
    g1: LineSegment [constr] StartX=-41.1657 StartY=-2.53692 StartZ=0 EndX=-44.5116 EndY=-3.14102 EndZ=0
    g2: LineSegment [constr] StartX=-41.1657 StartY=-2.53692 StartZ=0 EndX=-42.2479 EndY=-5.54839 EndZ=0
  constraints (8):
    c: Diameter(g0) = 1.8
    c: Coincident(g1,g0)
    c: Coincident(g2,g0)
    c: PointOnObject(g2,g-4)
    c: Angle(g1,g-3) = 1.5708
    c: Angle(g-4,g2) = 1.5708
    c: Distance(g1) = 3.4
    c: Distance(g2) = 3.2
FEATURE [PartDesign::Pad] Pad168
  BaseFeature = -> Pad167
  Direction = (1,0,0)
  Length = 5
  Length2 = 10
  Profile = -> Sketch258
  ReferenceAxis = -> Sketch258 [N_Axis]
  Refine = true
  Suppressed = false
  Type = 0
FEATURE [Sketcher::SketchObject] Sketch259
  ArcFitTolerance = 1e-06
  AttachmentSupport = -> [Pad168]
  ExternalGeometry = -> [Pad168]
  FullyConstrained = true
  MakeInternals = false
  MapMode = 5
  Placement = pos=(18,0,-4.7e-15) rot=(0.57735,-0.57735,-0.57735;2.0944rad)
  sketch-geometry (4):
    g0: LineSegment StartX=44.9561 StartY=0.0557565 StartZ=0 EndX=45.0825 EndY=0.755757 EndZ=0
    g1: LineSegment StartX=45.0825 StartY=0.755757 StartZ=0 EndX=42.7573 EndY=0.755757 EndZ=0
    g2: LineSegment StartX=42.7573 StartY=0.755757 StartZ=0 EndX=42.6309 EndY=0.0557565 EndZ=0
    g3: LineSegment StartX=42.6309 StartY=0.0557565 StartZ=0 EndX=44.9561 EndY=0.0557565 EndZ=0
  constraints (10):
    c: Coincident(g0,g-4)
    c: Coincident(g1,g0)
    c: Horizontal(g1)
    c: Coincident(g2,g1)
    c: Coincident(g3,g2)
    c: Coincident(g3,g0)
    c: Angle(g-3,g0) = 3.14159
    c: Parallel(g0,g2)
    c: Coincident(g2,g-4)
    c: DistanceY(g0,g0) = 0.7
FEATURE [PartDesign::Pad] Pad169
  BaseFeature = -> Pad168
  Direction = (-1,0,0)
  Length = 2.5
  Length2 = 10
  Profile = -> Sketch259
  ReferenceAxis = -> Sketch259 [N_Axis]
  Refine = true
  Reversed = true
  Suppressed = false
  Type = 0
FEATURE [Sketcher::SketchObject] Sketch260
  ArcFitTolerance = 1e-06
  AttachmentSupport = -> [Pad169]
  ExternalGeometry = -> [Pad169]
  FullyConstrained = true
  MakeInternals = false
  MapMode = 5
  Placement = pos=(20.5,0,0) rot=(0.57735,0.57735,0.57735;2.0944rad)
  sketch-geometry (4):
    g0: LineSegment StartX=-44.0825 StartY=0.755757 StartZ=0 EndX=-43.9561 EndY=0.0557565 EndZ=0
    g1: LineSegment StartX=-43.9561 StartY=0.0557565 StartZ=0 EndX=-42.6309 EndY=0.0557565 EndZ=0
    g2: LineSegment StartX=-42.6309 StartY=0.0557565 StartZ=0 EndX=-42.7573 EndY=0.755757 EndZ=0
    g3: LineSegment StartX=-42.7573 StartY=0.755757 StartZ=0 EndX=-44.0825 EndY=0.755757 EndZ=0
  constraints (10):
    c: PointOnObject(g0,g-4)
    c: PointOnObject(g0,g-6)
    c: Coincident(g1,g0)
    c: Coincident(g1,g-6)
    c: Coincident(g2,g1)
    c: Coincident(g2,g-4)
    c: Coincident(g3,g2)
    c: Coincident(g3,g0)
    c: Parallel(g0,g-5)
    c: DistanceX(g-5,g0) = 1
FEATURE [PartDesign::Pocket] Pocket119
  BaseFeature = -> Pad169
  Direction = (-1,0,0)
  Length = 1.5
  Length2 = 5
  Profile = -> Sketch260
  ReferenceAxis = -> Sketch260 [N_Axis]
  Refine = true
  Suppressed = false
  Type = 0
FEATURE [Sketcher::SketchObject] Sketch261
  ArcFitTolerance = 1e-06
  AttachmentOffset = pos=(0,0,6.5) rot=(0,0,1;0rad)
  AttachmentSupport = -> [Pocket119]
  ExternalGeometry = -> [Pocket119]
  FullyConstrained = true
  MakeInternals = false
  MapMode = 5
  Placement = pos=(0,-42.9313,1.4e-15) rot=(1,0,0;1.5708rad)
  sketch-geometry (3):
    g0: ArcOfCircle CenterX=30.85 CenterY=0.0557565 CenterZ=0 NormalX=0 NormalY=0 NormalZ=1 AngleXU=0 Radius=1.9 StartAngle=0 EndAngle=3.14159
    g1: LineSegment StartX=32.75 StartY=0.0557565 StartZ=0 EndX=32.75 EndY=0.0557582 EndZ=0
    g2: LineSegment StartX=32.75 StartY=0.0557582 StartZ=0 EndX=28.95 EndY=0.0557565 EndZ=0
  constraints (9):
    c: PointOnObject(g0,g-3)
    c: PointOnObject(g0,g-3)
    c: PointOnObject(g0,g-3)
    c: Diameter(g0) = 3.8
    c: Tangent(g1,g0) = -1.5708
    c: PointOnObject(g1,g0)
    c: Coincident(g2,g1)
    c: Coincident(g2,g0)
    c: DistanceX(g1,g-3) = 2
FEATURE [PartDesign::Pad] Pad170
  BaseFeature = -> Pocket119
  Direction = (0,-1,2e-16)
  Length = 1
  Length2 = 10
  Profile = -> Sketch261
  ReferenceAxis = -> Sketch261 [N_Axis]
  Refine = true
  Suppressed = false
  Type = 0
FEATURE [Sketcher::SketchObject] Sketch262
  ArcFitTolerance = 1e-06
  AttachmentSupport = -> [Pad170]
  ExternalGeometry = -> [Pad170]
  FullyConstrained = true
  MakeInternals = false
  MapMode = 5
  Placement = pos=(0,-43.9313,0) rot=(1,0,0;1.5708rad)
  sketch-geometry (2):
    g0: ArcOfCircle CenterX=30.85 CenterY=0.0557565 CenterZ=0 NormalX=0 NormalY=0 NormalZ=1 AngleXU=0 Radius=1.45 StartAngle=1.06273e-06 EndAngle=3.14159
    g1: LineSegment StartX=29.4 StartY=0.0557567 StartZ=0 EndX=32.3 EndY=0.055758 EndZ=0
  constraints (6):
    c: PointOnObject(g0,g-4)
    c: Diameter(g0) = 2.9
    c: Coincident(g0,g-3)
    c: PointOnObject(g0,g-4)
    c: Coincident(g1,g0)
    c: Coincident(g1,g0)
FEATURE [PartDesign::Pad] Pad171
  BaseFeature = -> Pad170
  Direction = (0,-1,2e-16)
  Length = 0.5
  Length2 = 10
  Profile = -> Sketch262
  ReferenceAxis = -> Sketch262 [N_Axis]
  Refine = true
  Suppressed = false
  Type = 0
FEATURE [PartDesign::Pad] Pad248
  BaseFeature = -> Pad171
  Direction = (1,0,0)
  Length = 0.05
  Length2 = 10
  Profile = -> Pad171 [Face43]
  Refine = true
  Suppressed = false
  Type = 0
FEATURE [Sketcher::SketchObject] Sketch345
  ArcFitTolerance = 1e-06
  AttachmentSupport = -> [Pad248]
  ExternalGeometry = -> [Pad248]
  FullyConstrained = true
  MakeInternals = false
  MapMode = 5
  Placement = pos=(0,-23.2313,0) rot=(0,0.707107,0.707107;3.14159rad)
  sketch-geometry (3):
    g0: LineSegment StartX=-23.3 StartY=-6.5 StartZ=0 EndX=-23.35 EndY=-6.5 EndZ=0
    g1: LineSegment StartX=-23.3 StartY=-6.5 StartZ=0 EndX=-23.35 EndY=-6.45 EndZ=0
    g2: LineSegment StartX=-23.35 StartY=-6.45 StartZ=0 EndX=-23.35 EndY=-6.5 EndZ=0
  constraints (7):
    c: Coincident(g0,g-3)
    c: Coincident(g0,g-4)
    c: Coincident(g1,g0)
    c: PointOnObject(g1,g-4)
    c: Coincident(g2,g1)
    c: Coincident(g2,g0)
    c: Angle(g-3,g1) = 3.14159
FEATURE [PartDesign::Pocket] Pocket162
  BaseFeature = -> Pad248
  Direction = (0,-1,2e-16)
  Length = 5
  Length2 = 5
  Profile = -> Sketch345
  ReferenceAxis = -> Sketch345 [N_Axis]
  Refine = true
  Suppressed = false
  Type = 0
FEATURE [PartDesign::Pad] Pad249
  BaseFeature = -> Pocket162
  Direction = (-1,0,0)
  Length = 0.05
  Length2 = 10
  Profile = -> Pocket162 [Face46]
  Refine = true
  Suppressed = false
  Type = 0
FEATURE [Sketcher::SketchObject] Sketch346
  ArcFitTolerance = 1e-06
  AttachmentSupport = -> [Pad249]
  ExternalGeometry = -> [Pad249]
  FullyConstrained = true
  MakeInternals = false
  MapMode = 5
  Placement = pos=(0,-39.505,0) rot=(1,0,0;1.5708rad)
  sketch-geometry (3):
    g0: LineSegment StartX=25.95 StartY=-5.2478 StartZ=0 EndX=25.9 EndY=-5.22961 EndZ=0
    g1: LineSegment StartX=25.9 StartY=-5.22961 StartZ=0 EndX=25.9 EndY=-5.2478 EndZ=0
    g2: LineSegment StartX=25.9 StartY=-5.2478 StartZ=0 EndX=25.95 EndY=-5.2478 EndZ=0
  constraints (7):
    c: Coincident(g0,g-3)
    c: PointOnObject(g0,g-5)
    c: Coincident(g1,g0)
    c: Coincident(g1,g-5)
    c: Coincident(g2,g-5)
    c: Coincident(g2,g-3)
    c: Angle(g-3,g0) = 3.14159
FEATURE [PartDesign::Pocket] Pocket163
  BaseFeature = -> Pad249
  Direction = (0,1,-2e-16)
  Length = 5
  Length2 = 5
  Profile = -> Sketch346
  ReferenceAxis = -> Sketch346 [N_Axis]
  Refine = true
  Suppressed = false
  Type = 0
FEATURE [PartDesign::Pad] Pad253
  BaseFeature = -> Pocket163
  Direction = (1,0,0)
  Length = 0.8
  Length2 = 10
  Profile = -> Pocket163 [Face58]
  Refine = true
  Suppressed = false
  Type = 0
FEATURE [Sketcher::SketchObject] Sketch349
  ArcFitTolerance = 1e-06
  AttachmentSupport = -> [Pad253]
  ExternalGeometry = -> [Pad253]
  FullyConstrained = true
  MakeInternals = false
  MapMode = 5
  Placement = pos=(31.25,0,0) rot=(0.57735,0.57735,0.57735;2.0944rad)
  sketch-geometry (1):
    g0: Circle CenterX=-35 CenterY=-1.99333 CenterZ=0 NormalX=0 NormalY=0 NormalZ=1 AngleXU=0 Radius=0.9
  constraints (2):
    c: Coincident(g0,g-3)
    c: Radius(g0) = 0.9
FEATURE [PartDesign::Pocket] Pocket166
  BaseFeature = -> Pad253
  Direction = (-1,0,0)
  Length = 5
  Length2 = 5
  Profile = -> Sketch349
  ReferenceAxis = -> Sketch349 [N_Axis]
  Refine = true
  Suppressed = false
  Type = 1
FEATURE [PartDesign::Body] Body016  label="Right_Inner_Leg"
  AllowCompound = false
  Group = -> [Binder010,Sketch246,Pad161,Sketch247,Pad162,Sketch248,Pad163,Sketch249,Pad164,Sketch250,Pocket114,Sketch251,Pocket115,Sketch252,Pad165,Sketch253,Pocket116,Sketch254,Pocket117,Sketch255,Pad166,Sketch256,Pocket118,Sketch257,Pad167,Sketch258,Pad168,Sketch259,Pad169,Sketch260,Pocket119,Sketch261,Pad170,Sketch262,Pad171,Pad248,Sketch345,Pocket162,Pad249,Sketch346,Pocket163,Pad253,Sketch349,Pocket166,+2 more]
  Origin = -> Origin017
  Placement = pos=(0,8.9e-15,0) rot=(0,0,1;0rad)
  Tip = -> Pocket167
COMPONENT P15 — recipe-attached ("Pre_Left_Inner_Leg", modeled in this document).
Construction recipe (the document's own serialized feature program — sketch geometry with constraints, then the solid features built on it; lengths are millimeters unless a unit is written):

FEATURE [PartDesign::SubShapeBinder] Binder011
  BindCopyOnChange = 0
  BindMode = 2
  ClaimChildren = false
  Context = -> Body017 [Binder011.]
  Fuse = false
  MakeFace = true
  OffsetFill = false
  OffsetIntersection = false
  OffsetJoinType = 0
  OffsetOpenResult = false
  PartialLoad = false
  Refine = true
  Relative = true
  _Version = 2
FEATURE [Sketcher::SketchObject] Sketch263
  ArcFitTolerance = 1e-06
  AttachmentSupport = -> [Binder011]
  ExternalGeometry = -> [Binder011]
  FullyConstrained = true
  MakeInternals = false
  MapMode = 5
  Placement = pos=(29.25,0,-7.6e-15) rot=(0.57735,0.57735,0.57735;2.0944rad)
  sketch-geometry (13):
    g0: LineSegment StartX=-33.5313 StartY=3 StartZ=0 EndX=-17.1313 EndY=3 EndZ=0
    g1: LineSegment StartX=-17.1313 StartY=3 StartZ=0 EndX=-17.1313 EndY=-9.8 EndZ=0
    g2: LineSegment StartX=-17.1313 StartY=-9.8 StartZ=0 EndX=-22.1313 EndY=-9.8 EndZ=0
    g3: ArcOfCircle CenterX=-26.2738 CenterY=-7 CenterZ=0 NormalX=0 NormalY=0 NormalZ=1 AngleXU=0 Radius=5 StartAngle=3.73598 EndAngle=5.6888
    g4: LineSegment StartX=-30.4162 StartY=-9.8 StartZ=0 EndX=-44.062 EndY=-4.89651 EndZ=0
    g5: LineSegment StartX=-42.095 StartY=-1.94424 StartZ=0 EndX=-33.5313 EndY=3 EndZ=0
    g6: LineSegment [constr] StartX=-26.2738 StartY=-12 StartZ=0 EndX=-17.1313 EndY=-12 EndZ=0
    g7: LineSegment [constr] StartX=-17.1313 StartY=-9.8 StartZ=0 EndX=-17.1313 EndY=-12 EndZ=0
    g8: LineSegment [constr] StartX=-26.2738 StartY=-7 StartZ=0 EndX=-26.2738 EndY=-12 EndZ=0
    g9: LineSegment StartX=-42.095 StartY=-1.94424 StartZ=0 EndX=-44.595 EndY=-1.94424 EndZ=0
    g10: LineSegment StartX=-44.062 StartY=-4.89651 StartZ=0 EndX=-44.595 EndY=-1.94424 EndZ=0
    g11: Circle CenterX=-35 CenterY=-1.99333 CenterZ=0 NormalX=0 NormalY=0 NormalZ=1 AngleXU=0 Radius=0.8
    g12: Circle CenterX=-26.2738 CenterY=-7 CenterZ=0 NormalX=0 NormalY=0 NormalZ=1 AngleXU=0 Radius=0.8
  constraints (41):
    c: Horizontal(g0)
    c: Coincident(g1,g0)
    c: Vertical(g1)
    c: Coincident(g2,g1)
    c: Horizontal(g2)
    c: Coincident(g3,g2)
    c: Coincident(g4,g3)
    c: Coincident(g5,g0)
    c: Radius(g3) = 5
    c: DistanceY(g1,g1) = 12.8
    c: DistanceY(g2,g3) = 0
    c: PointOnObject(g6,g3)
    c: Horizontal(g6)
    c: Coincident(g7,g1)
    c: Coincident(g7,g6)
    c: Vertical(g7)
    c: DistanceY(g7,g7) = 2.2
    c: PointOnObject(g-3,g1)
    c: PointOnObject(g0,g-4)
    c: DistanceX(g0,g0) = 16.4
    c: Parallel(g5,g-5)
    c: Coincident(g8,g3)
    c: Coincident(g8,g6)
    c: Vertical(g8)
    c: Coincident(g9,g5)
    c: Horizontal(g9)
    c: Coincident(g10,g4)
    c: Coincident(g10,g9)
    c: Distance(g4) = 14.5
    c: DistanceX(g9,g9) = 2.5
    c: Angle(g4,g10) = 2.0944
    c: Distance(g10) = 3
    c: DistanceX(g2,g2) = 5
    c: DistanceX(g4,g1) = 26.9307
    c: DistanceX(g9,g0) = 27.4637
    c: DistanceX(g-6,g0) = 17.8687
    c: DistanceY(g5,g0) = 4.94424
    c: Coincident(g11,g-6)
    c: Equal(g11,g-6)
    c: Coincident(g12,g3)
    c: Radius(g12) = 0.8
FEATURE [PartDesign::Pad] Pad172
  Direction = (1,0,0)
  Length = 2
  Length2 = 10
  Profile = -> Sketch263
  ReferenceAxis = -> Sketch263 [N_Axis]
  Refine = true
  Suppressed = false
  Type = 0
FEATURE [Sketcher::SketchObject] Sketch264
  ArcFitTolerance = 1e-06
  AttachmentSupport = -> [Pad172]
  ExternalGeometry = -> [Pad172]
  FullyConstrained = true
  MakeInternals = false
  MapMode = 5
  Placement = pos=(31.25,0,0) rot=(0.57735,0.57735,0.57735;2.0944rad)
  sketch-geometry (10):
    g0: LineSegment StartX=-17.1313 StartY=3 StartZ=0 EndX=-33.5313 EndY=3 EndZ=0
    g1: LineSegment StartX=-33.5313 StartY=3 StartZ=0 EndX=-42.095 EndY=-1.94424 EndZ=0
    g2: LineSegment StartX=-17.1313 StartY=3 StartZ=0 EndX=-17.1313 EndY=5 EndZ=0
    g3: LineSegment StartX=-17.1313 StartY=5 StartZ=0 EndX=-36.4313 EndY=5 EndZ=0
    g4: LineSegment StartX=-36.4313 StartY=5 StartZ=0 EndX=-36.4313 EndY=3.63509 EndZ=0
    g5: LineSegment StartX=-36.4313 StartY=3.63509 StartZ=0 EndX=-42.6309 EndY=0.0557565 EndZ=0
    g6: LineSegment StartX=-42.6309 StartY=0.0557565 StartZ=0 EndX=-44.9561 EndY=0.0557565 EndZ=0
    g7: LineSegment StartX=-44.595 StartY=-1.94424 StartZ=0 EndX=-44.9561 EndY=0.0557565 EndZ=0
    g8: LineSegment [constr] StartX=-36.7303 StartY=1.15303 StartZ=0 EndX=-37.7303 EndY=2.88509 EndZ=0
    g9: LineSegment StartX=-42.095 StartY=-1.94424 StartZ=0 EndX=-44.595 EndY=-1.94424 EndZ=0
  constraints (27):
    c: Coincident(g0,g-4)
    c: Coincident(g0,g-5)
    c: Coincident(g1,g0)
    c: Coincident(g1,g-6)
    c: Coincident(g2,g0)
    c: Vertical(g2)
    c: Coincident(g3,g2)
    c: Horizontal(g3)
    c: DistanceX(g3,g3) = 19.3
    c: DistanceY(g2,g2) = 2
    c: Coincident(g4,g3)
    c: Vertical(g4)
    c: Coincident(g5,g4)
    c: Coincident(g6,g5)
    c: Coincident(g7,g-7)
    c: Coincident(g7,g6)
    c: DistanceY(g1,g5) = 2
    c: PointOnObject(g8,g1)
    c: PointOnObject(g8,g5)
    c: Angle(g8,g1) = 1.5708
    c: Parallel(g1,g5)
    c: Horizontal(g6)
    c: Distance(g8) = 2
    c: Angle(g7,g-7) = 3.14159
    c: Coincident(g9,g1)
    c: Coincident(g9,g7)
    c: Distance(g4,g8) = 1.5
FEATURE [PartDesign::Pad] Pad173
  BaseFeature = -> Pad172
  Direction = (1,0,0)
  Length = 13.25
  Length2 = 10
  Profile = -> Sketch264
  ReferenceAxis = -> Sketch264 [N_Axis]
  Refine = true
  Reversed = true
  Suppressed = false
  Type = 0
FEATURE [Sketcher::SketchObject] Sketch265
  ArcFitTolerance = 1e-06
  AttachmentSupport = -> [Pad173]
  ExternalGeometry = -> [Pad173]
  FullyConstrained = true
  MakeInternals = false
  MapMode = 5
  Placement = pos=(18,0,0) rot=(0.57735,-0.57735,-0.57735;2.0944rad)
  sketch-geometry (9):
    g0: LineSegment StartX=33.5313 StartY=3 StartZ=0 EndX=42.095 EndY=-1.94424 EndZ=0
    g1: LineSegment StartX=42.095 StartY=-1.94424 StartZ=0 EndX=44.595 EndY=-1.94424 EndZ=0
    g2: LineSegment StartX=44.595 StartY=-1.94424 StartZ=0 EndX=44.062 EndY=-4.89651 EndZ=0
    g3: LineSegment StartX=44.062 StartY=-4.89651 StartZ=0 EndX=30.4162 EndY=-9.8 EndZ=0
    g4: LineSegment StartX=30.4162 StartY=-9.8 StartZ=0 EndX=22.1313 EndY=-9.8 EndZ=0
    g5: LineSegment StartX=22.1313 StartY=-9.8 StartZ=0 EndX=19.2313 EndY=-2 EndZ=0
    g6: LineSegment StartX=19.2313 StartY=-2 StartZ=0 EndX=23.2313 EndY=-2 EndZ=0
    g7: LineSegment StartX=23.2313 StartY=-2 StartZ=0 EndX=23.2313 EndY=3 EndZ=0
    g8: LineSegment StartX=33.5313 StartY=3 StartZ=0 EndX=23.2313 EndY=3 EndZ=0
  constraints (21):
    c: Coincident(g0,g-8)
    c: Coincident(g1,g0)
    c: Coincident(g1,g-8)
    c: Coincident(g2,g1)
    c: Coincident(g2,g-4)
    c: Coincident(g3,g2)
    c: Coincident(g3,g-4)
    c: Coincident(g4,g3)
    c: Coincident(g5,g4)
    c: Coincident(g6,g5)
    c: Horizontal(g6)
    c: Coincident(g7,g6)
    c: Vertical(g7)
    c: Coincident(g8,g0)
    c: PointOnObject(g8,g-6)
    c: Coincident(g7,g8)
    c: DistanceY(g7,g7) = 5
    c: DistanceX(g-9,g7) = 6.1
    c: DistanceX(g6,g6) = 4
    c: Coincident(g0,g-7)
    c: Coincident(g4,g-5)
FEATURE [PartDesign::Pad] Pad174
  BaseFeature = -> Pad173
  Direction = (-1,0,0)
  Length = 2
  Length2 = 10
  Profile = -> Sketch265
  ReferenceAxis = -> Sketch265 [N_Axis]
  Refine = true
  Reversed = true
  Suppressed = false
  Type = 0
FEATURE [Sketcher::SketchObject] Sketch266
  ArcFitTolerance = 1e-06
  AttachmentSupport = -> [Pad174]
  ExternalGeometry = -> [Pad174]
  FullyConstrained = true
  MakeInternals = false
  MapMode = 5
  Placement = pos=(20,0,0) rot=(0.57735,0.57735,0.57735;2.0944rad)
  sketch-geometry (4):
    g0: LineSegment StartX=-23.2313 StartY=3 StartZ=0 EndX=-25.2313 EndY=3 EndZ=0
    g1: LineSegment StartX=-25.2313 StartY=3 StartZ=0 EndX=-25.2313 EndY=-9.8 EndZ=0
    g2: LineSegment StartX=-25.2313 StartY=-9.8 StartZ=0 EndX=-23.2313 EndY=-9.8 EndZ=0
    g3: LineSegment StartX=-23.2313 StartY=-9.8 StartZ=0 EndX=-23.2313 EndY=3 EndZ=0
  constraints (11):
    c: Coincident(g0,g1)
    c: Coincident(g1,g2)
    c: Coincident(g2,g3)
    c: Coincident(g3,g0)
    c: Horizontal(g0)
    c: Horizontal(g2)
    c: Vertical(g1)
    c: Vertical(g3)
    c: Coincident(g0,g-3)
    c: PointOnObject(g1,g-4)
    c: DistanceX(g2,g2) = 2
FEATURE [PartDesign::Pad] Pad175
  BaseFeature = -> Pad174
  Direction = (1,0,0)
  Length = 3.3
  Length2 = 10
  Profile = -> Sketch266
  ReferenceAxis = -> Sketch266 [N_Axis]
  Refine = true
  Suppressed = false
  Type = 0
FEATURE [Sketcher::SketchObject] Sketch267
  ArcFitTolerance = 1e-06
  AttachmentSupport = -> [Pad175]
  ExternalGeometry = -> [Pad175]
  FullyConstrained = true
  MakeInternals = false
  MapMode = 5
  Placement = pos=(0,-23.2313,0) rot=(0,0.707107,0.707107;3.14159rad)
  sketch-geometry (3):
    g0: LineSegment StartX=-20 StartY=-9.8 StartZ=0 EndX=-23.3 EndY=-9.8 EndZ=0
    g1: LineSegment StartX=-23.3 StartY=-9.8 StartZ=0 EndX=-23.3 EndY=-6.5 EndZ=0
    g2: LineSegment StartX=-20 StartY=-9.8 StartZ=0 EndX=-23.3 EndY=-6.5 EndZ=0
  constraints (7):
    c: Coincident(g0,g-3)
    c: Coincident(g0,g-4)
    c: Coincident(g1,g0)
    c: PointOnObject(g1,g-4)
    c: Coincident(g2,g0)
    c: Coincident(g2,g1)
    c: Angle(g2,g0) = 0.785398
FEATURE [PartDesign::Pocket] Pocket120
  BaseFeature = -> Pad175
  Direction = (0,-1,2e-16)
  Length = 5
  Length2 = 5
  Profile = -> Sketch267
  ReferenceAxis = -> Sketch267 [N_Axis]
  Refine = true
  Suppressed = false
  Type = 0
FEATURE [Sketcher::SketchObject] Sketch268
  ArcFitTolerance = 1e-06
  AttachmentSupport = -> [Pocket120]
  ExternalGeometry = -> [Pocket120]
  FullyConstrained = true
  MakeInternals = false
  MapMode = 5
  Placement = pos=(20,0,0) rot=(0.57735,0.57735,0.57735;2.0944rad)
  sketch-geometry (1):
    g0: Circle CenterX=-35 CenterY=-1.99333 CenterZ=0 NormalX=0 NormalY=0 NormalZ=1 AngleXU=0 Radius=0.8
  constraints (2):
    c: Coincident(g0,g-3)
    c: Equal(g0,g-3)
FEATURE [PartDesign::Pocket] Pocket121
  BaseFeature = -> Pocket120
  Direction = (-1,0,0)
  Length = 5
  Length2 = 5
  Profile = -> Sketch268
  ReferenceAxis = -> Sketch268 [N_Axis]
  Refine = true
  Suppressed = false
  Type = 0
FEATURE [Sketcher::SketchObject] Sketch269
  ArcFitTolerance = 1e-06
  AttachmentSupport = -> [Pocket121]
  ExternalGeometry = -> [Pocket121]
  FullyConstrained = true
  MakeInternals = false
  MapMode = 5
  Placement = pos=(29.25,0,0) rot=(0.57735,-0.57735,-0.57735;2.0944rad)
  sketch-geometry (6):
    g0: LineSegment StartX=39.505 StartY=-0.448906 StartZ=0 EndX=39.505 EndY=-6.44891 EndZ=0
    g1: LineSegment StartX=39.505 StartY=-6.44891 StartZ=0 EndX=38.005 EndY=-6.44891 EndZ=0
    g2: LineSegment StartX=38.005 StartY=-6.44891 StartZ=0 EndX=38.005 EndY=0.417119 EndZ=0
    g3: LineSegment StartX=39.505 StartY=-0.448906 StartZ=0 EndX=38.005 EndY=0.417119 EndZ=0
    g4: GeomPoint [constr] X=39.505 Y=-6.44891 Z=0
    g5: GeomPoint [constr] X=38.005 Y=-6.44891 Z=0
  constraints (14):
    c: PointOnObject(g0,g-3)
    c: Vertical(g0)
    c: Horizontal(g1)
    c: Vertical(g2)
    c: Coincident(g3,g0)
    c: Coincident(g3,g2)
    c: DistanceX(g5,g4) = 1.5
    c: PointOnObject(g2,g-3)
    c: DistanceX(g0,g-3) = 2.59
    c: DistanceY(g0,g0) = 6
    c: Coincident(g1,g5)
    c: Coincident(g2,g1)
    c: Coincident(g1,g4)
    c: Coincident(g0,g1)
FEATURE [PartDesign::Pad] Pad176
  BaseFeature = -> Pocket121
  Direction = (-1,0,0)
  Length = 3.3
  Length2 = 10
  Profile = -> Sketch269
  ReferenceAxis = -> Sketch269 [N_Axis]
  Refine = true
  Suppressed = false
  Type = 0
FEATURE [Sketcher::SketchObject] Sketch270
  ArcFitTolerance = 1e-06
  AttachmentSupport = -> [Pad176]
  ExternalGeometry = -> [Pad176]
  FullyConstrained = true
  MakeInternals = false
  MapMode = 5
  Placement = pos=(0,-38.005,0) rot=(0,0.707107,0.707107;3.14159rad)
  sketch-geometry (3):
    g0: LineSegment StartX=-29.25 StartY=-6.44891 StartZ=0 EndX=-25.95 EndY=-6.44891 EndZ=0
    g1: LineSegment StartX=-25.95 StartY=-6.44891 StartZ=0 EndX=-25.95 EndY=-5.2478 EndZ=0
    g2: LineSegment StartX=-25.95 StartY=-5.2478 StartZ=0 EndX=-29.25 EndY=-6.44891 EndZ=0
  constraints (7):
    c: Coincident(g0,g-4)
    c: Coincident(g0,g-4)
    c: Coincident(g1,g-3)
    c: PointOnObject(g1,g-3)
    c: Coincident(g2,g1)
    c: Coincident(g2,g-4)
    c: Angle(g0,g2) = 0.349066
FEATURE [PartDesign::Pocket] Pocket122
  BaseFeature = -> Pad176
  Direction = (0,-1,2e-16)
  Length = 5
  Length2 = 5
  Profile = -> Sketch270
  ReferenceAxis = -> Sketch270 [N_Axis]
  Refine = true
  Suppressed = false
  Type = 0
FEATURE [Sketcher::SketchObject] Sketch271
  ArcFitTolerance = 1e-06
  AttachmentSupport = -> [Pocket122]
  ExternalGeometry = -> [Pocket122]
  FullyConstrained = true
  MakeInternals = false
  MapMode = 5
  Placement = pos=(0,0,5) rot=(0,0,1;0rad)
  sketch-geometry (1):
    g0: Circle CenterX=24.25 CenterY=-28.2313 CenterZ=0 NormalX=0 NormalY=0 NormalZ=1 AngleXU=0 Radius=1
  constraints (3):
    c: Radius(g0) = 1
    c: DistanceX(g-5,g0) = 6.25
    c: DistanceY(g0,g-5) = 11.1
FEATURE [PartDesign::Pocket] Pocket123
  BaseFeature = -> Pocket122
  Direction = (0,0,-1)
  Length = 5
  Length2 = 5
  Profile = -> Sketch271
  ReferenceAxis = -> Sketch271 [N_Axis]
  Refine = true
  Suppressed = false
  Type = 0
FEATURE [Sketcher::SketchObject] Sketch272
  ArcFitTolerance = 1e-06
  AttachmentSupport = -> [Pocket123]
  ExternalGeometry = -> [Pocket123]
  FullyConstrained = true
  MakeInternals = false
  MapMode = 5
  Placement = pos=(31.25,0,0) rot=(0.57735,0.57735,0.57735;2.0944rad)
  sketch-geometry (24):
    g0: LineSegment StartX=-36.4313 StartY=5 StartZ=0 EndX=-17.1313 EndY=5 EndZ=0
    g1: LineSegment StartX=-17.1313 StartY=5 StartZ=0 EndX=-17.1313 EndY=-9.8 EndZ=0
    g2: LineSegment StartX=-36.4313 StartY=5 StartZ=0 EndX=-36.4313 EndY=3.63509 EndZ=0
    g3: LineSegment StartX=-36.4313 StartY=3.63509 StartZ=0 EndX=-42.6309 EndY=0.0557565 EndZ=0
    g4: LineSegment StartX=-42.6309 StartY=0.0557565 StartZ=0 EndX=-44.9561 EndY=0.0557565 EndZ=0
    g5: LineSegment StartX=-44.9561 StartY=0.0557565 StartZ=0 EndX=-44.062 EndY=-4.89651 EndZ=0
    g6: LineSegment StartX=-44.062 StartY=-4.89651 StartZ=0 EndX=-32.8313 EndY=-8.93216 EndZ=0
    g7: LineSegment StartX=-32.8313 StartY=-8.93216 StartZ=0 EndX=-32.8313 EndY=-3.6 EndZ=0
    g8: LineSegment StartX=-32.8313 StartY=-3.6 StartZ=0 EndX=-28.8813 EndY=0.35 EndZ=0
    g9: LineSegment StartX=-28.8813 StartY=0.35 StartZ=0 EndX=-22.7813 EndY=0.35 EndZ=0
    g10: LineSegment StartX=-22.7813 StartY=0.35 StartZ=0 EndX=-18.8313 EndY=-3.6 EndZ=0
    g11: LineSegment StartX=-18.8313 StartY=-3.6 StartZ=0 EndX=-18.8313 EndY=-9.8 EndZ=0
    g12: LineSegment StartX=-17.1313 StartY=-9.8 StartZ=0 EndX=-18.8313 EndY=-9.8 EndZ=0
    g13: LineSegment StartX=-34.5313 StartY=3 StartZ=0 EndX=-28.6355 EndY=3 EndZ=0
    g14: LineSegment StartX=-28.6355 StartY=3 StartZ=0 EndX=-34.5313 EndY=-2.89584 EndZ=0
    g15: LineSegment StartX=-34.5313 StartY=-2.89584 StartZ=0 EndX=-34.5313 EndY=-6.19607 EndZ=0
    g16: LineSegment StartX=-34.5313 StartY=-6.19607 StartZ=0 EndX=-41.7556 EndY=-3.60007 EndZ=0
    g17: LineSegment StartX=-42.1528 StartY=-1.40026 StartZ=0 EndX=-34.5313 EndY=3 EndZ=0
    g18: Circle CenterX=-19.7813 CenterY=2.15 CenterZ=0 NormalX=0 NormalY=0 NormalZ=1 AngleXU=0 Radius=1.45
    g19: LineSegment [constr] StartX=-29.5884 StartY=-0.357107 StartZ=0 EndX=-30.7905 EndY=0.844975 EndZ=0
    g20: LineSegment [constr] StartX=-36.5473 StartY=1.83605 StartZ=0 EndX=-37.2973 EndY=3.13509 EndZ=0
    g21: LineSegment [constr] StartX=-40.8145 StartY=-3.93824 StartZ=0 EndX=-41.4909 EndY=-5.82041 EndZ=0
    g22: LineSegment StartX=-41.7556 StartY=-3.60007 StartZ=0 EndX=-42.1528 EndY=-1.40026 EndZ=0
    g23: LineSegment [constr] StartX=-41.9751 StartY=-2.38435 StartZ=0 EndX=-44.4353 EndY=-2.82854 EndZ=0
  constraints (69):
    c: Coincident(g0,g-4)
    c: Coincident(g0,g-10)
    c: Coincident(g1,g0)
    c: Coincident(g1,g-10)
    c: Coincident(g2,g0)
    c: Coincident(g2,g-5)
    c: Coincident(g3,g2)
    c: Coincident(g3,g-6)
    c: Coincident(g4,g3)
    c: Coincident(g4,g-7)
    c: Coincident(g5,g4)
    c: Coincident(g5,g-8)
    c: Coincident(g6,g5)
    c: PointOnObject(g6,g-8)
    c: Coincident(g7,g6)
    c: Vertical(g7)
    c: Coincident(g8,g7)
    c: Coincident(g9,g8)
    c: Horizontal(g9)
    c: Coincident(g10,g9)
    c: Coincident(g11,g10)
    c: PointOnObject(g11,g-9)
    c: Vertical(g11)
    c: Coincident(g12,g1)
    c: Coincident(g12,g11)
    c: Horizontal(g13)
    c: Coincident(g14,g13)
    c: Coincident(g15,g14)
    c: Vertical(g15)
    c: Coincident(g16,g15)
    c: Coincident(g17,g13)
    c: Diameter(g18) = 2.9
    c: DistanceX(g18,g0) = 2.65
    c: DistanceY(g18,g0) = 2.85
    c: DistanceX(g12,g12) = 1.7
    c: Angle(g10,g11) = 2.35619
    c: Angle(g8,g9) = 2.35619
    c: DistanceX(g9,g9) = 6.1
    c: DistanceY(g11,g11) = 6.2
    c: DistanceY(g7,g10) = 0
    c: DistanceX(g6,g11) = 14
    c: Parallel(g8,g14)
    c: PointOnObject(g19,g8)
    c: PointOnObject(g19,g14)
    c: Angle(g19,g8) = 1.5708
    c: Distance(g19) = 1.7
    c: Distance(g8,g19) = 1
    c: Parallel(g17,g3)
    c: Parallel(g16,g6)
    c: PointOnObject(g20,g17)
    c: PointOnObject(g20,g3)
    c: PointOnObject(g21,g16)
    c: PointOnObject(g21,g6)
    c: Angle(g21,g16) = 1.5708
    c: Angle(g3,g20) = 1.5708
    c: Distance(g20,g2) = 1
    c: Distance(g21,g16) = 1
    c: Distance(g21) = 2
    c: Distance(g20) = 1.5
    c: DistanceY(g13,g0) = 2
    c: DistanceX(g15,g7) = 1.7
    c: Coincident(g22,g16)
    c: Coincident(g22,g17)
    c: Parallel(g5,g22)
    c: PointOnObject(g23,g22)
    c: PointOnObject(g23,g5)
    c: Angle(g23,g22) = 1.5708
    c: Distance(g23) = 2.5
    c: Distance(g23,g17) = 1
FEATURE [PartDesign::Pad] Pad177
  BaseFeature = -> Pocket123
  Direction = (1,0,0)
  Length = 3.5
  Length2 = 10
  Profile = -> Sketch272
  ReferenceAxis = -> Sketch272 [N_Axis]
  Refine = true
  Suppressed = false
  Type = 0
FEATURE [Sketcher::SketchObject] Sketch273
  ArcFitTolerance = 1e-06
  AttachmentSupport = -> [Pad177]
  ExternalGeometry = -> [Pad177]
  FullyConstrained = true
  MakeInternals = false
  MapMode = 5
  Placement = pos=(34.75,0,0) rot=(0.57735,0.57735,0.57735;2.0944rad)
  sketch-geometry (1):
    g0: Circle CenterX=-35 CenterY=-1.99333 CenterZ=0 NormalX=0 NormalY=0 NormalZ=1 AngleXU=0 Radius=2
  constraints (3):
    c: Radius(g-3) = 0.8
    c: Coincident(g0,g-3)
    c: Radius(g0) = 2
FEATURE [PartDesign::Pocket] Pocket124
  BaseFeature = -> Pad177
  Direction = (-1,0,0)
  Length = 1.5
  Length2 = 5
  Profile = -> Sketch273
  ReferenceAxis = -> Sketch273 [N_Axis]
  Refine = true
  Suppressed = false
  Type = 0
FEATURE [Sketcher::SketchObject] Sketch274
  ArcFitTolerance = 1e-06
  AttachmentSupport = -> [Pocket124]
  ExternalGeometry = -> [Pocket124]
  FullyConstrained = true
  MakeInternals = false
  MapMode = 5
  Placement = pos=(31.25,0,0) rot=(0.57735,0.57735,0.57735;2.0944rad)
  sketch-geometry (2):
    g0: Circle CenterX=-26.2738 CenterY=-7 CenterZ=0 NormalX=0 NormalY=0 NormalZ=1 AngleXU=0 Radius=0.8
    g1: Circle CenterX=-26.2738 CenterY=-7 CenterZ=0 NormalX=0 NormalY=0 NormalZ=1 AngleXU=0 Radius=2.25
  constraints (4):
    c: Coincident(g0,g-3)
    c: Equal(g0,g-3)
    c: Coincident(g1,g0)
    c: Radius(g1) = 2.25
FEATURE [PartDesign::Pad] Pad178
  BaseFeature = -> Pocket124
  Direction = (1,0,0)
  Length = 2
  Length2 = 10
  Profile = -> Sketch274
  ReferenceAxis = -> Sketch274 [N_Axis]
  Refine = true
  Suppressed = false
  Type = 0
FEATURE [Sketcher::SketchObject] Sketch275
  ArcFitTolerance = 1e-06
  AttachmentSupport = -> [Pad178]
  ExternalGeometry = -> [Pad178]
  FullyConstrained = false
  MakeInternals = false
  MapMode = 5
  Placement = pos=(31.25,0,0) rot=(0.57735,0.57735,0.57735;2.0944rad)
  sketch-geometry (3):
    g0: Circle CenterX=-41.1657 CenterY=-2.53692 CenterZ=0 NormalX=0 NormalY=0 NormalZ=1 AngleXU=0 Radius=0.9
    g1: LineSegment [constr] StartX=-41.1657 StartY=-2.53692 StartZ=0 EndX=-44.5116 EndY=-3.14102 EndZ=0
    g2: LineSegment [constr] StartX=-41.1657 StartY=-2.53692 StartZ=0 EndX=-42.2479 EndY=-5.54839 EndZ=0
  constraints (8):
    c: Diameter(g0) = 1.8
    c: Coincident(g1,g0)
    c: Coincident(g2,g0)
    c: PointOnObject(g2,g-4)
    c: Angle(g1,g-3) = 1.5708
    c: Angle(g-4,g2) = 1.5708
    c: Distance(g1) = 3.4
    c: Distance(g2) = 3.2
FEATURE [PartDesign::Pad] Pad179
  BaseFeature = -> Pad178
  Direction = (1,0,0)
  Length = 5
  Length2 = 10
  Profile = -> Sketch275
  ReferenceAxis = -> Sketch275 [N_Axis]
  Refine = true
  Suppressed = false
  Type = 0
FEATURE [Sketcher::SketchObject] Sketch276
  ArcFitTolerance = 1e-06
  AttachmentSupport = -> [Pad179]
  ExternalGeometry = -> [Pad179]
  FullyConstrained = true
  MakeInternals = false
  MapMode = 5
  Placement = pos=(18,0,-4.7e-15) rot=(0.57735,-0.57735,-0.57735;2.0944rad)
  sketch-geometry (4):
    g0: LineSegment StartX=44.9561 StartY=0.0557565 StartZ=0 EndX=45.0825 EndY=0.755757 EndZ=0
    g1: LineSegment StartX=45.0825 StartY=0.755757 StartZ=0 EndX=42.7573 EndY=0.755757 EndZ=0
    g2: LineSegment StartX=42.7573 StartY=0.755757 StartZ=0 EndX=42.6309 EndY=0.0557565 EndZ=0
    g3: LineSegment StartX=42.6309 StartY=0.0557565 StartZ=0 EndX=44.9561 EndY=0.0557565 EndZ=0
  constraints (10):
    c: Coincident(g0,g-4)
    c: Coincident(g1,g0)
    c: Horizontal(g1)
    c: Coincident(g2,g1)
    c: Coincident(g3,g2)
    c: Coincident(g3,g0)
    c: Angle(g-3,g0) = 3.14159
    c: Parallel(g0,g2)
    c: Coincident(g2,g-4)
    c: DistanceY(g0,g0) = 0.7
FEATURE [PartDesign::Pad] Pad180
  BaseFeature = -> Pad179
  Direction = (-1,0,0)
  Length = 2.5
  Length2 = 10
  Profile = -> Sketch276
  ReferenceAxis = -> Sketch276 [N_Axis]
  Refine = true
  Reversed = true
  Suppressed = false
  Type = 0
FEATURE [Sketcher::SketchObject] Sketch277
  ArcFitTolerance = 1e-06
  AttachmentSupport = -> [Pad180]
  ExternalGeometry = -> [Pad180]
  FullyConstrained = true
  MakeInternals = false
  MapMode = 5
  Placement = pos=(20.5,0,0) rot=(0.57735,0.57735,0.57735;2.0944rad)
  sketch-geometry (4):
    g0: LineSegment StartX=-44.0825 StartY=0.755757 StartZ=0 EndX=-43.9561 EndY=0.0557565 EndZ=0
    g1: LineSegment StartX=-43.9561 StartY=0.0557565 StartZ=0 EndX=-42.6309 EndY=0.0557565 EndZ=0
    g2: LineSegment StartX=-42.6309 StartY=0.0557565 StartZ=0 EndX=-42.7573 EndY=0.755757 EndZ=0
    g3: LineSegment StartX=-42.7573 StartY=0.755757 StartZ=0 EndX=-44.0825 EndY=0.755757 EndZ=0
  constraints (10):
    c: PointOnObject(g0,g-4)
    c: PointOnObject(g0,g-6)
    c: Coincident(g1,g0)
    c: Coincident(g1,g-6)
    c: Coincident(g2,g1)
    c: Coincident(g2,g-4)
    c: Coincident(g3,g2)
    c: Coincident(g3,g0)
    c: Parallel(g0,g-5)
    c: DistanceX(g-5,g0) = 1
FEATURE [PartDesign::Pocket] Pocket125
  BaseFeature = -> Pad180
  Direction = (-1,0,0)
  Length = 1.5
  Length2 = 5
  Profile = -> Sketch277
  ReferenceAxis = -> Sketch277 [N_Axis]
  Refine = true
  Suppressed = false
  Type = 0
FEATURE [PartDesign::Pad] Pad250
  BaseFeature = -> Pocket125
  Direction = (-1,0,0)
  Length = 0.05
  Length2 = 10
  Profile = -> Pocket125 [Face45]
  Refine = true
  Suppressed = false
  Type = 0
FEATURE [Sketcher::SketchObject] Sketch347
  ArcFitTolerance = 1e-06
  AttachmentSupport = -> [Pad250]
  ExternalGeometry = -> [Pad250]
  FullyConstrained = true
  MakeInternals = false
  MapMode = 5
  Placement = pos=(0,-39.505,0) rot=(1,0,0;1.5708rad)
  sketch-geometry (3):
    g0: LineSegment StartX=25.95 StartY=-5.2478 StartZ=0 EndX=25.9 EndY=-5.2478 EndZ=0
    g1: LineSegment StartX=25.9 StartY=-5.2478 StartZ=0 EndX=25.9 EndY=-5.22961 EndZ=0
    g2: LineSegment StartX=25.95 StartY=-5.2478 StartZ=0 EndX=25.9 EndY=-5.22961 EndZ=0
  constraints (7):
    c: Coincident(g0,g-4)
    c: Coincident(g0,g-5)
    c: Coincident(g1,g-5)
    c: PointOnObject(g1,g-5)
    c: Coincident(g2,g-4)
    c: Coincident(g2,g1)
    c: Angle(g-3,g2) = 3.14159
FEATURE [PartDesign::Pocket] Pocket164
  BaseFeature = -> Pad250
  Direction = (0,1,-2e-16)
  Length = 5
  Length2 = 5
  Profile = -> Sketch347
  ReferenceAxis = -> Sketch347 [N_Axis]
  Refine = true
  Suppressed = false
  Type = 0
FEATURE [PartDesign::Pad] Pad251
  BaseFeature = -> Pocket164
  Direction = (1,0,0)
  Length = 0.05
  Length2 = 10
  Profile = -> Pocket164 [Face42]
  Refine = true
  Suppressed = false
  Type = 0
FEATURE [Sketcher::SketchObject] Sketch348
  ArcFitTolerance = 1e-06
  AttachmentSupport = -> [Pad251]
  ExternalGeometry = -> [Pad251]
  FullyConstrained = true
  MakeInternals = false
  MapMode = 5
  Placement = pos=(0,-25.2313,0) rot=(1,0,0;1.5708rad)
  sketch-geometry (3):
    g0: LineSegment StartX=23.3 StartY=-6.5 StartZ=0 EndX=23.35 EndY=-6.45 EndZ=0
    g1: LineSegment StartX=23.35 StartY=-6.45 StartZ=0 EndX=23.35 EndY=-6.5 EndZ=0
    g2: LineSegment StartX=23.35 StartY=-6.5 StartZ=0 EndX=23.3 EndY=-6.5 EndZ=0
  constraints (7):
    c: Coincident(g0,g-5)
    c: PointOnObject(g0,g-3)
    c: Coincident(g1,g0)
    c: Coincident(g1,g-4)
    c: Coincident(g2,g1)
    c: Coincident(g2,g0)
    c: Angle(g-5,g0) = 3.14159
FEATURE [PartDesign::Pocket] Pocket165
  BaseFeature = -> Pad251
  Direction = (0,1,-2e-16)
  Length = 5
  Length2 = 5
  Profile = -> Sketch348
  ReferenceAxis = -> Sketch348 [N_Axis]
  Refine = true
  Suppressed = false
  Type = 0
FEATURE [PartDesign::Pad] Pad252
  BaseFeature = -> Pocket165
  Direction = (1,0,0)
  Length = 0.8
  Length2 = 10
  Profile = -> Pocket165 [Face54]
  Refine = true
  Suppressed = false
  Type = 0
FEATURE [Sketcher::SketchObject] Sketch351
  ArcFitTolerance = 1e-06
  AttachmentSupport = -> [Pad252]
  ExternalGeometry = -> [Pad252]
  FullyConstrained = true
  MakeInternals = false
  MapMode = 5
  Placement = pos=(31.25,0,0) rot=(0.57735,0.57735,0.57735;2.0944rad)
  sketch-geometry (1):
    g0: Circle CenterX=-35 CenterY=-1.99333 CenterZ=0 NormalX=0 NormalY=0 NormalZ=1 AngleXU=0 Radius=0.9
  constraints (2):
    c: Coincident(g0,g-3)
    c: Radius(g0) = 0.9
FEATURE [PartDesign::Pocket] Pocket168
  BaseFeature = -> Pad252
  Direction = (-1,0,0)
  Length = 5
  Length2 = 5
  Profile = -> Sketch351
  ReferenceAxis = -> Sketch351 [N_Axis]
  Refine = true
  Suppressed = false
  Type = 1
FEATURE [Sketcher::SketchObject] Sketch352
  ArcFitTolerance = 1e-06
  AttachmentSupport = -> [Pocket168]
  ExternalGeometry = -> [Pocket168]
  FullyConstrained = true
  MakeInternals = false
  MapMode = 5
  Placement = pos=(33.25,0,0) rot=(0.57735,0.57735,0.57735;2.0944rad)
  sketch-geometry (1):
    g0: Circle CenterX=-26.2738 CenterY=-7 CenterZ=0 NormalX=0 NormalY=0 NormalZ=1 AngleXU=0 Radius=0.9
  constraints (2):
    c: Coincident(g0,g-3)
    c: Radius(g0) = 0.9
FEATURE [PartDesign::Pocket] Pocket169
  BaseFeature = -> Pocket168
  Direction = (-1,0,0)
  Length = 4
  Length2 = 5
  Profile = -> Sketch352
  ReferenceAxis = -> Sketch352 [N_Axis]
  Refine = true
  Suppressed = false
  Type = 0
FEATURE [PartDesign::Body] Body017  label="Pre_Left_Inner_Leg"
  AllowCompound = false
  Group = -> [Binder011,Sketch263,Pad172,Sketch264,Pad173,Sketch265,Pad174,Sketch266,Pad175,Sketch267,Pocket120,Sketch268,Pocket121,Sketch269,Pad176,Sketch270,Pocket122,Sketch271,Pocket123,Sketch272,Pad177,Sketch273,Pocket124,Sketch274,Pad178,Sketch275,Pad179,Sketch276,Pad180,Sketch277,Pocket125,Pad250,Sketch347,Pocket164,Pad251,Sketch348,Pocket165,Pad252,Sketch351,Pocket168,Sketch352,Pocket169]
  Origin = -> Origin018
  Tip = -> Pocket169
COMPONENT P16 — recipe-attached ("Right_Outer_Leg", modeled in this document).
Construction recipe (the document's own serialized feature program — sketch geometry with constraints, then the solid features built on it; lengths are millimeters unless a unit is written):

FEATURE [PartDesign::SubShapeBinder] Binder012
  BindCopyOnChange = 0
  BindMode = 0
  ClaimChildren = false
  Context = -> Body018 [Binder012.]
  Fuse = false
  MakeFace = true
  OffsetFill = false
  OffsetIntersection = false
  OffsetJoinType = 0
  OffsetOpenResult = false
  PartialLoad = false
  Refine = true
  Relative = true
  Support = -> [Body016[Pad171.Face23]]
  _Version = 2
FEATURE [Sketcher::SketchObject] Sketch278
  ArcFitTolerance = 1e-06
  AttachmentSupport = -> [Binder012]
  ExternalGeometry = -> [Binder012]
  FullyConstrained = true
  MakeInternals = false
  MapMode = 5
  Placement = pos=(0,0,5) rot=(0,0,1;0rad)
  sketch-geometry (5):
    g0: LineSegment StartX=18 StartY=-17.1313 StartZ=0 EndX=18 EndY=-36.4313 EndZ=0
    g1: LineSegment StartX=18 StartY=-36.4313 StartZ=0 EndX=36.25 EndY=-36.4313 EndZ=0
    g2: LineSegment StartX=36.25 StartY=-36.4313 StartZ=0 EndX=36.25 EndY=-17.1313 EndZ=0
    g3: LineSegment StartX=36.25 StartY=-17.1313 StartZ=0 EndX=18 EndY=-17.1313 EndZ=0
    g4: Circle CenterX=24.25 CenterY=-28.2313 CenterZ=0 NormalX=0 NormalY=0 NormalZ=1 AngleXU=0 Radius=0.75
  constraints (13):
    c: Coincident(g0,g1)
    c: Coincident(g1,g2)
    c: Coincident(g2,g3)
    c: Coincident(g3,g0)
    c: Vertical(g0)
    c: Vertical(g2)
    c: Horizontal(g1)
    c: Horizontal(g3)
    c: Coincident(g0,g-6)
    c: PointOnObject(g-7,g1)
    c: DistanceX(g-5,g2) = 1.5
    c: Coincident(g4,g-3)
    c: Radius(g4) = 0.75
FEATURE [PartDesign::Pad] Pad181
  Direction = (0,0,1)
  Length = 1.5
  Length2 = 10
  Profile = -> Sketch278
  ReferenceAxis = -> Sketch278 [N_Axis]
  Refine = true
  Suppressed = false
  Type = 0
FEATURE [Sketcher::SketchObject] Sketch279
  ArcFitTolerance = 1e-06
  AttachmentSupport = -> [Pad181]
  ExternalGeometry = -> [Pad181]
  FullyConstrained = true
  MakeInternals = false
  MapMode = 5
  Placement = pos=(0,-17.1313,0) rot=(0,0.707107,0.707107;3.14159rad)
  sketch-geometry (6):
    g0: LineSegment StartX=-18 StartY=6.5 StartZ=0 EndX=-18 EndY=3 EndZ=0
    g1: LineSegment StartX=-18 StartY=3 StartZ=0 EndX=-29.25 EndY=3 EndZ=0
    g2: LineSegment StartX=-29.25 StartY=3 StartZ=0 EndX=-29.25 EndY=-9.8 EndZ=0
    g3: LineSegment StartX=-29.25 StartY=-9.8 StartZ=0 EndX=-36.25 EndY=-9.8 EndZ=0
    g4: LineSegment StartX=-36.25 StartY=-9.8 StartZ=0 EndX=-36.25 EndY=6.5 EndZ=0
    g5: LineSegment StartX=-36.25 StartY=6.5 StartZ=0 EndX=-18 EndY=6.5 EndZ=0
  constraints (16):
    c: Coincident(g0,g-4)
    c: Vertical(g0)
    c: Coincident(g1,g0)
    c: Horizontal(g1)
    c: Coincident(g2,g1)
    c: Vertical(g2)
    c: Coincident(g3,g2)
    c: Horizontal(g3)
    c: Coincident(g4,g3)
    c: Coincident(g4,g-6)
    c: Coincident(g5,g4)
    c: Coincident(g5,g0)
    c: Vertical(g4)
    c: DistanceY(g0,g0) = 3.5
    c: DistanceY(g2,g2) = 12.8
    c: DistanceX(g1,g1) = 11.25
FEATURE [PartDesign::Pad] Pad182
  BaseFeature = -> Pad181
  Direction = (0,1,-2e-16)
  Length = 1.5
  Length2 = 10
  Profile = -> Sketch279
  ReferenceAxis = -> Sketch279 [N_Axis]
  Refine = true
  Suppressed = false
  Type = 0
FEATURE [Sketcher::SketchObject] Sketch280
  ArcFitTolerance = 1e-06
  AttachmentSupport = -> [Pad182]
  ExternalGeometry = -> [Pad182]
  FullyConstrained = true
  MakeInternals = false
  MapMode = 5
  Placement = pos=(36.25,1.31e-14,-1.66e-14) rot=(0.57735,0.57735,0.57735;2.0944rad)
  sketch-geometry (13):
    g0: LineSegment StartX=-36.4313 StartY=5 StartZ=0 EndX=-17.1313 EndY=5 EndZ=0
    g1: LineSegment StartX=-17.1313 StartY=5 StartZ=0 EndX=-17.1313 EndY=-9.8 EndZ=0
    g2: LineSegment StartX=-17.1313 StartY=-9.8 StartZ=0 EndX=-18.8313 EndY=-9.8 EndZ=0
    g3: LineSegment StartX=-18.8313 StartY=-9.8 StartZ=0 EndX=-18.8313 EndY=-3.6 EndZ=0
    g4: LineSegment StartX=-18.8313 StartY=-3.6 StartZ=0 EndX=-22.784 EndY=0.352727 EndZ=0
    g5: LineSegment StartX=-22.784 StartY=0.352727 StartZ=0 EndX=-28.884 EndY=0.352727 EndZ=0
    g6: LineSegment StartX=-28.884 StartY=0.352727 StartZ=0 EndX=-32.8368 EndY=-3.6 EndZ=0
    g7: LineSegment StartX=-32.8368 StartY=-3.6 StartZ=0 EndX=-32.8368 EndY=-8.93 EndZ=0
    g8: LineSegment StartX=-32.8368 StartY=-8.93 StartZ=0 EndX=-44.0636 EndY=-4.89473 EndZ=0
    g9: LineSegment StartX=-44.0636 StartY=-4.89473 StartZ=0 EndX=-44.9569 EndY=0.0553024 EndZ=0
    g10: LineSegment StartX=-44.9569 StartY=0.0553024 StartZ=0 EndX=-36.4313 EndY=6.5 EndZ=0
    g11: LineSegment StartX=-36.4313 StartY=6.5 StartZ=0 EndX=-36.4313 EndY=5 EndZ=0
    g12: Circle CenterX=-41.1636 CenterY=-2.53473 CenterZ=0 NormalX=0 NormalY=0 NormalZ=1 AngleXU=0 Radius=0.95
  constraints (36):
    c: Coincident(g0,g-3)
    c: Coincident(g0,g-4)
    c: Coincident(g1,g0)
    c: Coincident(g1,g-4)
    c: Coincident(g2,g1)
    c: Horizontal(g2)
    c: Coincident(g3,g2)
    c: Vertical(g3)
    c: Coincident(g4,g3)
    c: Coincident(g5,g4)
    c: Horizontal(g5)
    c: Coincident(g6,g5)
    c: Coincident(g7,g6)
    c: Vertical(g7)
    c: Coincident(g8,g7)
    c: Coincident(g9,g8)
    c: Coincident(g10,g9)
    c: Coincident(g11,g10)
    c: Coincident(g11,g0)
    c: Vertical(g11)
    c: DistanceX(g2,g2) = 1.7
    c: DistanceY(g3,g3) = 6.2
    c: DistanceX(g5,g5) = 6.1
    c: Angle(g4,g3) = 2.35619
    c: Angle(g6,g5) = 2.35619
    c: Distance(g4) = 5.59
    c: Distance(g6) = 5.59
    c: DistanceY(g11,g11) = 1.5
    c: DistanceY(g7,g7) = 5.33
    c: Distance(g8) = 11.93
    c: Angle(g7,g8) = 1.22574
    c: Distance(g9) = 5.03
    c: Angle(g8,g9) = 2.0944
    c: Radius(g12) = 0.95
    c: DistanceX(g8,g12) = 2.9
    c: DistanceY(g8,g12) = 2.36
FEATURE [PartDesign::Pad] Pad183
  BaseFeature = -> Pad182
  Direction = (1,0,0)
  Length = 1.5
  Length2 = 10
  Profile = -> Sketch280
  ReferenceAxis = -> Sketch280 [N_Axis]
  Refine = true
  Reversed = true
  Suppressed = false
  Type = 0
FEATURE [Sketcher::SketchObject] Sketch281
  ArcFitTolerance = 1e-06
  AttachmentSupport = -> [Pad183]
  ExternalGeometry = -> [Pad183]
  FullyConstrained = true
  MakeInternals = false
  MapMode = 5
  Placement = pos=(0,0,6.5) rot=(0,0,1;0rad)
  sketch-geometry (4):
    g0: LineSegment StartX=36.25 StartY=-15.6313 StartZ=0 EndX=34.75 EndY=-15.6313 EndZ=0
    g1: LineSegment StartX=34.75 StartY=-15.6313 StartZ=0 EndX=34.75 EndY=-36.4313 EndZ=0
    g2: LineSegment StartX=34.75 StartY=-36.4313 StartZ=0 EndX=36.25 EndY=-36.4313 EndZ=0
    g3: LineSegment StartX=36.25 StartY=-36.4313 StartZ=0 EndX=36.25 EndY=-15.6313 EndZ=0
  constraints (10):
    c: Coincident(g0,g1)
    c: Coincident(g1,g2)
    c: Coincident(g2,g3)
    c: Coincident(g3,g0)
    c: Horizontal(g0)
    c: Horizontal(g2)
    c: Vertical(g1)
    c: Vertical(g3)
    c: Coincident(g0,g-5)
    c: Coincident(g1,g-4)
FEATURE [PartDesign::Pad] Pad184
  BaseFeature = -> Pad183
  Direction = (0,0,1)
  Length = 2
  Length2 = 10
  Profile = -> Sketch281
  ReferenceAxis = -> Sketch281 [N_Axis]
  Refine = true
  Suppressed = false
  Type = 0
FEATURE [Sketcher::SketchObject] Sketch282
  ArcFitTolerance = 1e-06
  AttachmentSupport = -> [Pad184]
  ExternalGeometry = -> [Pad184]
  FullyConstrained = true
  MakeInternals = false
  MapMode = 5
  Placement = pos=(36.25,0,0) rot=(0.57735,0.57735,0.57735;2.0944rad)
  sketch-geometry (6):
    g0: LineSegment StartX=-15.6313 StartY=8.5 StartZ=0 EndX=-15.6313 EndY=6.5 EndZ=0
    g1: LineSegment StartX=-15.6313 StartY=8.5 StartZ=0 EndX=-17.6313 EndY=8.5 EndZ=0
    g2: LineSegment StartX=-17.6313 StartY=8.5 StartZ=0 EndX=-15.6313 EndY=6.5 EndZ=0
    g3: LineSegment StartX=-36.4313 StartY=6.5 StartZ=0 EndX=-36.4313 EndY=8.5 EndZ=0
    g4: LineSegment StartX=-36.4313 StartY=8.5 StartZ=0 EndX=-33.7855 EndY=8.5 EndZ=0
    g5: LineSegment StartX=-33.7855 StartY=8.5 StartZ=0 EndX=-36.4313 EndY=6.5 EndZ=0
  constraints (15):
    c: Coincident(g0,g-6)
    c: PointOnObject(g0,g-6)
    c: Coincident(g1,g0)
    c: PointOnObject(g1,g-4)
    c: Coincident(g2,g1)
    c: Coincident(g2,g0)
    c: Coincident(g3,g-5)
    c: Coincident(g3,g-4)
    c: Coincident(g4,g3)
    c: PointOnObject(g4,g-4)
    c: Coincident(g5,g4)
    c: Coincident(g5,g3)
    c: Angle(g-5,g5) = 3.14159
    c: DistanceY(g0,g0) = 2
    c: DistanceX(g1,g1) = 2
FEATURE [PartDesign::Pocket] Pocket126
  BaseFeature = -> Pad184
  Direction = (-1,0,0)
  Length = 5
  Length2 = 5
  Profile = -> Sketch282
  ReferenceAxis = -> Sketch282 [N_Axis]
  Refine = true
  Suppressed = false
  Type = 0
FEATURE [Sketcher::SketchObject] Sketch283
  ArcFitTolerance = 1e-06
  AttachmentSupport = -> [Pocket126]
  FullyConstrained = true
  MakeInternals = false
  MapMode = 5
  Placement = pos=(0,0,6.5) rot=(0,0,1;0rad)
  sketch-geometry (1):
    g0: Circle CenterX=24.25 CenterY=-28.2313 CenterZ=0 NormalX=0 NormalY=0 NormalZ=1 AngleXU=0 Radius=2.6
  constraints (2):
    c: Coincident(g0,g-3)
    c: Diameter(g0) = 5.2
FEATURE [PartDesign::Pad] Pad185
  BaseFeature = -> Pocket126
  Direction = (0,0,1)
  Length = 4
  Length2 = 10
  Profile = -> Sketch283
  ReferenceAxis = -> Sketch283 [N_Axis]
  Refine = true
  Suppressed = false
  Type = 0
FEATURE [PartDesign::Pocket] Pocket127
  BaseFeature = -> Pad185
  Direction = (0,0,1)
  Length = 2
  Length2 = 5
  Profile = -> Pad185 [Face27]
  Refine = true
  Suppressed = false
  Type = 0
FEATURE [Sketcher::SketchObject] Sketch284
  ArcFitTolerance = 1e-06
  AttachmentSupport = -> [Pocket127]
  ExternalGeometry = -> [Pocket127]
  FullyConstrained = true
  MakeInternals = false
  MapMode = 5
  Placement = pos=(0,0,6.5) rot=(0,0,1;0rad)
  sketch-geometry (4):
    g0: LineSegment StartX=26.85 StartY=-28.2313 StartZ=0 EndX=26.85 EndY=-34.0313 EndZ=0
    g1: LineSegment StartX=26.85 StartY=-34.0313 StartZ=0 EndX=32.65 EndY=-34.0313 EndZ=0
    g2: LineSegment StartX=32.65 StartY=-34.0313 StartZ=0 EndX=32.65 EndY=-28.2313 EndZ=0
    g3: LineSegment StartX=32.65 StartY=-28.2313 StartZ=0 EndX=26.85 EndY=-28.2313 EndZ=0
  constraints (11):
    c: Coincident(g0,g1)
    c: Coincident(g1,g2)
    c: Coincident(g2,g3)
    c: Coincident(g3,g0)
    c: Vertical(g0)
    c: Vertical(g2)
    c: Horizontal(g1)
    c: Horizontal(g3)
    c: Coincident(g0,g-4)
    c: DistanceX(g3,g3) = 5.8
    c: DistanceY(g2,g2) = 5.8
FEATURE [PartDesign::Pad] Pad186
  BaseFeature = -> Pocket127
  Direction = (0,0,1)
  Length = 4
  Length2 = 10
  Profile = -> Sketch284
  ReferenceAxis = -> Sketch284 [N_Axis]
  Refine = true
  Suppressed = false
  Type = 0
FEATURE [Sketcher::SketchObject] Sketch285
  ArcFitTolerance = 1e-06
  AttachmentSupport = -> [Pad186]
  ExternalGeometry = -> [Pad186]
  FullyConstrained = true
  MakeInternals = false
  MapMode = 5
  Placement = pos=(0,0,6.5) rot=(0,0,1;0rad)
  sketch-geometry (4):
    g0: LineSegment [constr] StartX=24.25 StartY=-28.2313 StartZ=0 EndX=24.25 EndY=-30.8313 EndZ=0
    g1: LineSegment StartX=24.25 StartY=-30.8313 StartZ=0 EndX=26.85 EndY=-30.8313 EndZ=0
    g2: LineSegment StartX=26.85 StartY=-30.8313 StartZ=0 EndX=26.85 EndY=-28.2313 EndZ=0
    g3: ArcOfCircle CenterX=24.25 CenterY=-28.2313 CenterZ=0 NormalX=0 NormalY=0 NormalZ=1 AngleXU=0 Radius=2.6 StartAngle=4.71239 EndAngle=6.28319
  constraints (11):
    c: Coincident(g0,g-3)
    c: PointOnObject(g0,g-3)
    c: Vertical(g0)
    c: Coincident(g1,g0)
    c: PointOnObject(g1,g-5)
    c: Horizontal(g1)
    c: Coincident(g2,g1)
    c: Coincident(g2,g-5)
    c: Coincident(g3,g2)
    c: Coincident(g3,g0)
    c: Tangent(g3,g-3)
FEATURE [PartDesign::Pad] Pad187
  BaseFeature = -> Pad186
  Direction = (0,0,1)
  Length = 4
  Length2 = 10
  Profile = -> Sketch285
  ReferenceAxis = -> Sketch285 [N_Axis]
  Refine = true
  Suppressed = false
  Type = 0
FEATURE [Sketcher::SketchObject] Sketch286
  ArcFitTolerance = 1e-06
  AttachmentSupport = -> [Pad187]
  ExternalGeometry = -> [Pad187]
  FullyConstrained = true
  MakeInternals = false
  MapMode = 5
  Placement = pos=(0,0,10.5) rot=(0,0,1;0rad)
  sketch-geometry (1):
    g0: Circle CenterX=29.75 CenterY=-31.1313 CenterZ=0 NormalX=0 NormalY=0 NormalZ=1 AngleXU=0 Radius=1.45
  constraints (4):
    c: DistanceX(g-3,g-3) = 5.8
    c: DistanceX(g0,g-4) = 2.9
    c: DistanceY(g0,g-4) = 2.9
    c: Radius(g0) = 1.45
FEATURE [PartDesign::Pocket] Pocket128
  BaseFeature = -> Pad187
  Direction = (0,0,-1)
  Length = 4
  Length2 = 5
  Profile = -> Sketch286
  ReferenceAxis = -> Sketch286 [N_Axis]
  Refine = true
  Suppressed = false
  Type = 0
FEATURE [Sketcher::SketchObject] Sketch287
  ArcFitTolerance = 1e-06
  AttachmentSupport = -> [Pocket128]
  ExternalGeometry = -> [Pocket128]
  FullyConstrained = true
  MakeInternals = false
  MapMode = 5
  Placement = pos=(36.25,0,0) rot=(0.57735,0.57735,0.57735;2.0944rad)
  sketch-geometry (9):
    g0: LineSegment StartX=-15.6313 StartY=3.5 StartZ=0 EndX=-15.6313 EndY=3.3 EndZ=0
    g1: LineSegment StartX=-15.6313 StartY=3.3 StartZ=0 EndX=-28.884 EndY=3.3 EndZ=0
    g2: LineSegment StartX=-28.884 StartY=3.3 StartZ=0 EndX=-32.3287 EndY=-0.144698 EndZ=0
    g3: LineSegment StartX=-32.3287 StartY=-0.144698 StartZ=0 EndX=-44.9208 EndY=-0.144698 EndZ=0
    g4: LineSegment StartX=-44.9208 StartY=-0.144698 StartZ=0 EndX=-44.9569 EndY=0.0553024 EndZ=0
    g5: LineSegment StartX=-44.9569 StartY=0.0553024 StartZ=0 EndX=-32.4116 EndY=0.0553024 EndZ=0
    g6: LineSegment StartX=-32.4116 StartY=0.0553024 StartZ=0 EndX=-28.9669 EndY=3.5 EndZ=0
    g7: LineSegment StartX=-28.9669 StartY=3.5 StartZ=0 EndX=-15.6313 EndY=3.5 EndZ=0
    g8: LineSegment [constr] StartX=-29.5326 StartY=2.65147 StartZ=0 EndX=-29.674 EndY=2.79289 EndZ=0
  constraints (27):
    c: PointOnObject(g0,g-8)
    c: PointOnObject(g0,g-8)
    c: Coincident(g1,g0)
    c: Horizontal(g1)
    c: Coincident(g2,g1)
    c: Coincident(g3,g2)
    c: PointOnObject(g3,g-4)
    c: Horizontal(g3)
    c: Coincident(g4,g3)
    c: Coincident(g5,g4)
    c: Horizontal(g5)
    c: Coincident(g6,g5)
    c: Coincident(g7,g6)
    c: Coincident(g7,g0)
    c: Horizontal(g7)
    c: DistanceY(g0,g0) = 0.2
    c: DistanceY(g0,g-8) = 3
    c: DistanceX(g1,g-7) = 0
    c: Coincident(g4,g-4)
    c: Parallel(g2,g6)
    c: PointOnObject(g8,g2)
    c: PointOnObject(g8,g6)
    c: Angle(g6,g8) = 1.5708
    c: Distance(g8) = 0.2
    c: Angle(g2,g1) = 2.35619
    c: DistanceY(g2,g5) = 0.2
    c: Distance(g8,g6) = 1
FEATURE [PartDesign::Pocket] Pocket129
  BaseFeature = -> Pocket128
  Direction = (-1,0,0)
  Length = 0.3
  Length2 = 5
  Profile = -> Sketch287
  ReferenceAxis = -> Sketch287 [N_Axis]
  Refine = true
  Suppressed = false
  Type = 0
FEATURE [PartDesign::Body] Body018  label="Right_Outer_Leg"
  AllowCompound = false
  Group = -> [Binder012,Sketch278,Pad181,Sketch279,Pad182,Sketch280,Pad183,Sketch281,Pad184,Sketch282,Pocket126,Sketch283,Pad185,Pocket127,Sketch284,Pad186,Sketch285,Pad187,Sketch286,Pocket128,Sketch287,Pocket129]
  Origin = -> Origin019
  Placement = pos=(0,8.9e-15,0) rot=(0,0,1;0rad)
  Tip = -> Pocket129
